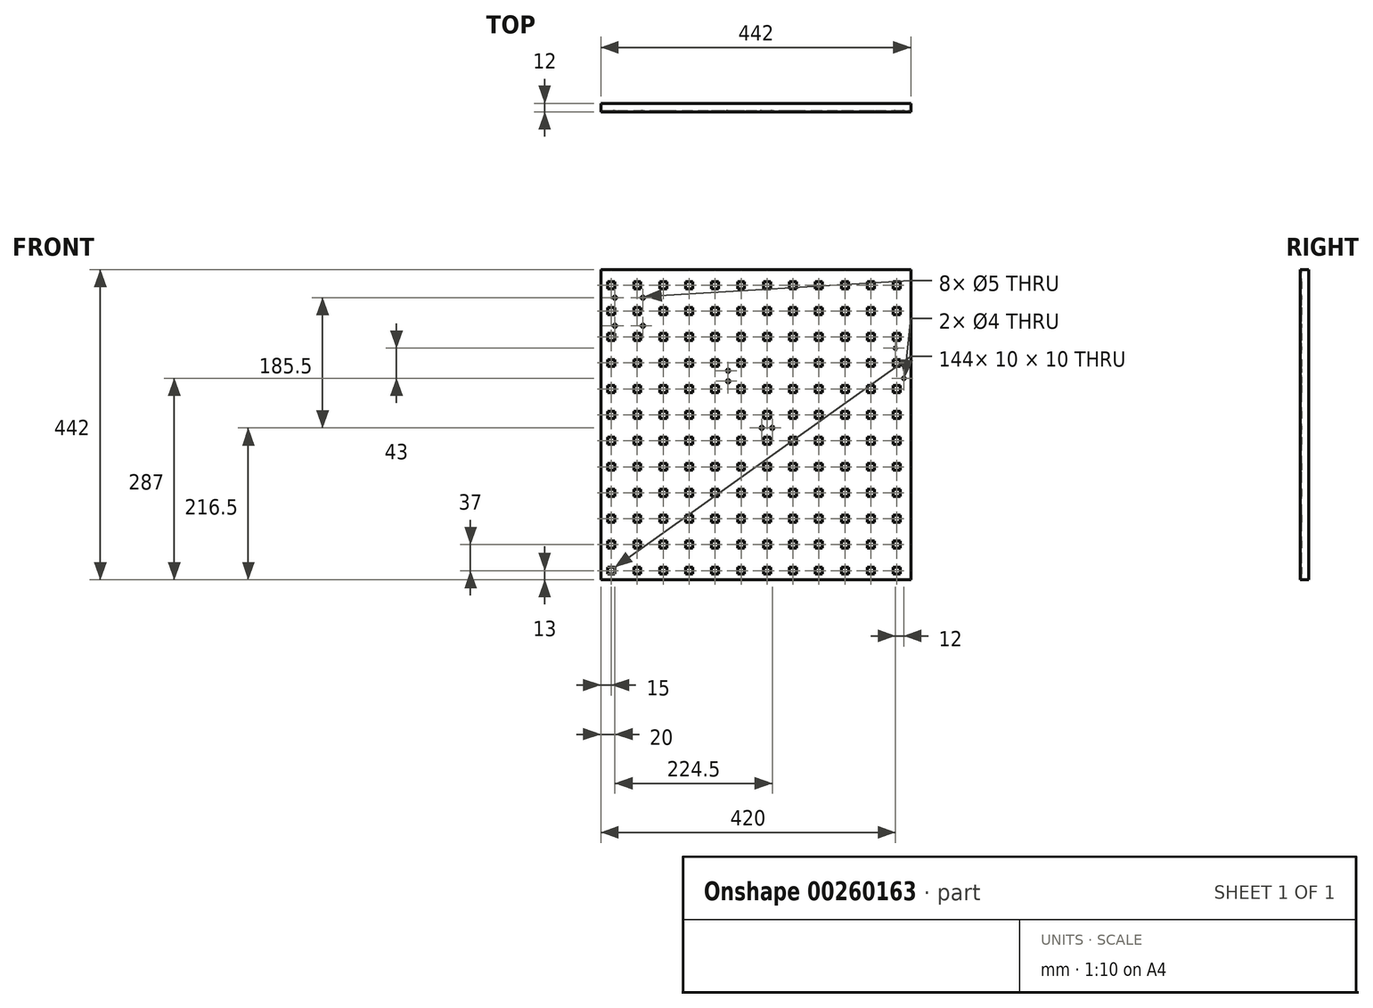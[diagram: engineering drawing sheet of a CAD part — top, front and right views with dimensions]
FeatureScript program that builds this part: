
annotation { "Feature Type Name" : "Feature", "Feature Type Description" : "" }
export const myFeature = defineFeature(function(context is Context, id is Id, definition is map)
    precondition{}
    {
        {
            var Q0;
            Q0=qCreatedBy(makeId("Front.planeOp"),FACE);
            var sketch = newSketch(context, id + "F0", { "sketchPlane" : qUnion([Q0])});
            skLineSegment(sketch, "E0.bottom", {"start": v(221, -221) * mm, "end": v(-221, -221) * mm});
            skLineSegment(sketch, "E0.top", {"start": v(221, 221) * mm, "end": v(-221, 221) * mm});
            skLineSegment(sketch, "E0.left", {"start": v(221, -221) * mm, "end": v(221, 221) * mm});
            skLineSegment(sketch, "E0.right", {"start": v(-221, -221) * mm, "end": v(-221, 221) * mm});
            skPoint(sketch, "E0.middle", {"position": v(0, 0) * mm});
            skSolve(sketch);
        }
        {
            var Q0;
            Q0=makeQuery(id+"F0.imprint","IMPRINT",FACE,{"disambiguationData":[TD([[makeQuery(id+"F0.imprint","IMPRINT",EDGE,{"derivedFrom":sQuery(id+"F0.wireOp",EDGE,"E0.bottom")}),-1.0]])]});
            extrude(context, id + "F1", {"entities" : qUnion([Q0]), "depth" : 12 * mm});
        }
        {
            var Q0;
            Q0=makeQuery(id+"F1.opExtrude","CAP_FACE",FACE,{"disambiguationData":[OSD([sQuery(id+"F0.wireOp",EDGE,"E0.bottom"),sQuery(id+"F0.wireOp",EDGE,"E0.top"),sQuery(id+"F0.wireOp",EDGE,"E0.left"),sQuery(id+"F0.wireOp",EDGE,"E0.right")])],"isStart":true});
            var sketch = newSketch(context, id + "F2", { "sketchPlane" : qUnion([Q0])});
            skLineSegment(sketch, "E1.bottom", {"start": v(220.5, -220.5) * mm, "end": v(-220.5, -220.5) * mm});
            skLineSegment(sketch, "E1.top", {"start": v(220.5, 220.5) * mm, "end": v(-220.5, 220.5) * mm});
            skLineSegment(sketch, "E1.left", {"start": v(220.5, -220.5) * mm, "end": v(220.5, 220.5) * mm});
            skLineSegment(sketch, "E1.right", {"start": v(-220.5, -220.5) * mm, "end": v(-220.5, 220.5) * mm});
            skPoint(sketch, "E1.middle", {"position": v(0, 0) * mm});
            skSolve(sketch);
        }
        {
            var Q0;
            Q0=makeQuery(id+"F2.imprint","IMPRINT",FACE,{"disambiguationData":[TD([[makeQuery(id+"F2.imprint","IMPRINT",EDGE,{"derivedFrom":sQuery(id+"F2.wireOp",EDGE,"E1.bottom")}),-1.0]])]});
            extrude(context, id + "F3", {"entities" : qUnion([Q0]), "operationType" : NewBodyOperationType.REMOVE, "oppositeDirection" : true, "depth" : 10 * mm});
        }
        {
            var Q0;
            Q0=makeQuery(id+"F1.opExtrude","CAP_FACE",FACE,{"disambiguationData":[OSD([sQuery(id+"F0.wireOp",EDGE,"E0.bottom"),sQuery(id+"F0.wireOp",EDGE,"E0.top"),sQuery(id+"F0.wireOp",EDGE,"E0.left"),sQuery(id+"F0.wireOp",EDGE,"E0.right")])],"isStart":false});
            var sketch = newSketch(context, id + "F4", { "sketchPlane" : qUnion([Q0])});
            skLineSegment(sketch, "E2.bottom", {"start": v(-201, 194) * mm, "end": v(-211, 194) * mm});
            skLineSegment(sketch, "E2.top", {"start": v(-201, 204) * mm, "end": v(-211, 204) * mm});
            skLineSegment(sketch, "E2.left", {"start": v(-201, 194) * mm, "end": v(-201, 204) * mm});
            skLineSegment(sketch, "E2.right", {"start": v(-211, 194) * mm, "end": v(-211, 204) * mm});
            skPoint(sketch, "E2.middle", {"position": v(-206, 199) * mm});
            skLineSegment(sketch, "E3.0.1.0", {"start": v(-201, 157) * mm, "end": v(-211, 157) * mm});
            skPoint(sketch, "E3.0.1.1", {"position": v(-206, 162) * mm});
            skLineSegment(sketch, "E3.0.1.2", {"start": v(-211, 157) * mm, "end": v(-211, 167) * mm});
            skLineSegment(sketch, "E3.0.1.3", {"start": v(-201, 167) * mm, "end": v(-211, 167) * mm});
            skLineSegment(sketch, "E3.0.1.4", {"start": v(-201, 157) * mm, "end": v(-201, 167) * mm});
            skLineSegment(sketch, "E3.1.0.0", {"start": v(-164, 194) * mm, "end": v(-174, 194) * mm});
            skPoint(sketch, "E3.1.0.1", {"position": v(-169, 199) * mm});
            skLineSegment(sketch, "E3.1.0.2", {"start": v(-174, 194) * mm, "end": v(-174, 204) * mm});
            skLineSegment(sketch, "E3.1.0.3", {"start": v(-164, 204) * mm, "end": v(-174, 204) * mm});
            skLineSegment(sketch, "E3.1.0.4", {"start": v(-164, 194) * mm, "end": v(-164, 204) * mm});
            skLineSegment(sketch, "E3.1.1.0", {"start": v(-164, 157) * mm, "end": v(-174, 157) * mm});
            skPoint(sketch, "E3.1.1.1", {"position": v(-169, 162) * mm});
            skLineSegment(sketch, "E3.1.1.2", {"start": v(-174, 157) * mm, "end": v(-174, 167) * mm});
            skLineSegment(sketch, "E3.1.1.3", {"start": v(-164, 167) * mm, "end": v(-174, 167) * mm});
            skLineSegment(sketch, "E3.1.1.4", {"start": v(-164, 157) * mm, "end": v(-164, 167) * mm});
            skLineSegment(sketch, "E3.2.0.0", {"start": v(-127, 194) * mm, "end": v(-137, 194) * mm});
            skPoint(sketch, "E3.2.0.1", {"position": v(-132, 199) * mm});
            skLineSegment(sketch, "E3.2.0.2", {"start": v(-137, 194) * mm, "end": v(-137, 204) * mm});
            skLineSegment(sketch, "E3.2.0.3", {"start": v(-127, 204) * mm, "end": v(-137, 204) * mm});
            skLineSegment(sketch, "E3.2.0.4", {"start": v(-127, 194) * mm, "end": v(-127, 204) * mm});
            skLineSegment(sketch, "E3.2.1.0", {"start": v(-127, 157) * mm, "end": v(-137, 157) * mm});
            skPoint(sketch, "E3.2.1.1", {"position": v(-132, 162) * mm});
            skLineSegment(sketch, "E3.2.1.2", {"start": v(-137, 157) * mm, "end": v(-137, 167) * mm});
            skLineSegment(sketch, "E3.2.1.3", {"start": v(-127, 167) * mm, "end": v(-137, 167) * mm});
            skLineSegment(sketch, "E3.2.1.4", {"start": v(-127, 157) * mm, "end": v(-127, 167) * mm});
            skLineSegment(sketch, "E3.3.0.0", {"start": v(-90, 194) * mm, "end": v(-100, 194) * mm});
            skPoint(sketch, "E3.3.0.1", {"position": v(-95, 199) * mm});
            skLineSegment(sketch, "E3.3.0.2", {"start": v(-100, 194) * mm, "end": v(-100, 204) * mm});
            skLineSegment(sketch, "E3.3.0.3", {"start": v(-90, 204) * mm, "end": v(-100, 204) * mm});
            skLineSegment(sketch, "E3.3.0.4", {"start": v(-90, 194) * mm, "end": v(-90, 204) * mm});
            skLineSegment(sketch, "E3.3.1.0", {"start": v(-90, 157) * mm, "end": v(-100, 157) * mm});
            skPoint(sketch, "E3.3.1.1", {"position": v(-95, 162) * mm});
            skLineSegment(sketch, "E3.3.1.2", {"start": v(-100, 157) * mm, "end": v(-100, 167) * mm});
            skLineSegment(sketch, "E3.3.1.3", {"start": v(-90, 167) * mm, "end": v(-100, 167) * mm});
            skLineSegment(sketch, "E3.3.1.4", {"start": v(-90, 157) * mm, "end": v(-90, 167) * mm});
            skLineSegment(sketch, "E3.4.0.0", {"start": v(-53, 194) * mm, "end": v(-63, 194) * mm});
            skPoint(sketch, "E3.4.0.1", {"position": v(-58, 199) * mm});
            skLineSegment(sketch, "E3.4.0.2", {"start": v(-63, 194) * mm, "end": v(-63, 204) * mm});
            skLineSegment(sketch, "E3.4.0.3", {"start": v(-53, 204) * mm, "end": v(-63, 204) * mm});
            skLineSegment(sketch, "E3.4.0.4", {"start": v(-53, 194) * mm, "end": v(-53, 204) * mm});
            skLineSegment(sketch, "E3.4.1.0", {"start": v(-53, 157) * mm, "end": v(-63, 157) * mm});
            skPoint(sketch, "E3.4.1.1", {"position": v(-58, 162) * mm});
            skLineSegment(sketch, "E3.4.1.2", {"start": v(-63, 157) * mm, "end": v(-63, 167) * mm});
            skLineSegment(sketch, "E3.4.1.3", {"start": v(-53, 167) * mm, "end": v(-63, 167) * mm});
            skLineSegment(sketch, "E3.4.1.4", {"start": v(-53, 157) * mm, "end": v(-53, 167) * mm});
            skLineSegment(sketch, "E3.5.0.0", {"start": v(-16, 194) * mm, "end": v(-26, 194) * mm});
            skPoint(sketch, "E3.5.0.1", {"position": v(-21, 199) * mm});
            skLineSegment(sketch, "E3.5.0.2", {"start": v(-26, 194) * mm, "end": v(-26, 204) * mm});
            skLineSegment(sketch, "E3.5.0.3", {"start": v(-16, 204) * mm, "end": v(-26, 204) * mm});
            skLineSegment(sketch, "E3.5.0.4", {"start": v(-16, 194) * mm, "end": v(-16, 204) * mm});
            skLineSegment(sketch, "E3.5.1.0", {"start": v(-16, 157) * mm, "end": v(-26, 157) * mm});
            skPoint(sketch, "E3.5.1.1", {"position": v(-21, 162) * mm});
            skLineSegment(sketch, "E3.5.1.2", {"start": v(-26, 157) * mm, "end": v(-26, 167) * mm});
            skLineSegment(sketch, "E3.5.1.3", {"start": v(-16, 167) * mm, "end": v(-26, 167) * mm});
            skLineSegment(sketch, "E3.5.1.4", {"start": v(-16, 157) * mm, "end": v(-16, 167) * mm});
            skLineSegment(sketch, "E3.6.0.0", {"start": v(21, 194) * mm, "end": v(11, 194) * mm});
            skPoint(sketch, "E3.6.0.1", {"position": v(16, 199) * mm});
            skLineSegment(sketch, "E3.6.0.2", {"start": v(11, 194) * mm, "end": v(11, 204) * mm});
            skLineSegment(sketch, "E3.6.0.3", {"start": v(21, 204) * mm, "end": v(11, 204) * mm});
            skLineSegment(sketch, "E3.6.0.4", {"start": v(21, 194) * mm, "end": v(21, 204) * mm});
            skLineSegment(sketch, "E3.6.1.0", {"start": v(21, 157) * mm, "end": v(11, 157) * mm});
            skPoint(sketch, "E3.6.1.1", {"position": v(16, 162) * mm});
            skLineSegment(sketch, "E3.6.1.2", {"start": v(11, 157) * mm, "end": v(11, 167) * mm});
            skLineSegment(sketch, "E3.6.1.3", {"start": v(21, 167) * mm, "end": v(11, 167) * mm});
            skLineSegment(sketch, "E3.6.1.4", {"start": v(21, 157) * mm, "end": v(21, 167) * mm});
            skLineSegment(sketch, "E3.7.0.0", {"start": v(58, 194) * mm, "end": v(48, 194) * mm});
            skPoint(sketch, "E3.7.0.1", {"position": v(53, 199) * mm});
            skLineSegment(sketch, "E3.7.0.2", {"start": v(48, 194) * mm, "end": v(48, 204) * mm});
            skLineSegment(sketch, "E3.7.0.3", {"start": v(58, 204) * mm, "end": v(48, 204) * mm});
            skLineSegment(sketch, "E3.7.0.4", {"start": v(58, 194) * mm, "end": v(58, 204) * mm});
            skLineSegment(sketch, "E3.7.1.0", {"start": v(58, 157) * mm, "end": v(48, 157) * mm});
            skPoint(sketch, "E3.7.1.1", {"position": v(53, 162) * mm});
            skLineSegment(sketch, "E3.7.1.2", {"start": v(48, 157) * mm, "end": v(48, 167) * mm});
            skLineSegment(sketch, "E3.7.1.3", {"start": v(58, 167) * mm, "end": v(48, 167) * mm});
            skLineSegment(sketch, "E3.7.1.4", {"start": v(58, 157) * mm, "end": v(58, 167) * mm});
            skLineSegment(sketch, "E3.8.0.0", {"start": v(95, 194) * mm, "end": v(85, 194) * mm});
            skPoint(sketch, "E3.8.0.1", {"position": v(90, 199) * mm});
            skLineSegment(sketch, "E3.8.0.2", {"start": v(85, 194) * mm, "end": v(85, 204) * mm});
            skLineSegment(sketch, "E3.8.0.3", {"start": v(95, 204) * mm, "end": v(85, 204) * mm});
            skLineSegment(sketch, "E3.8.0.4", {"start": v(95, 194) * mm, "end": v(95, 204) * mm});
            skLineSegment(sketch, "E3.8.1.0", {"start": v(95, 157) * mm, "end": v(85, 157) * mm});
            skPoint(sketch, "E3.8.1.1", {"position": v(90, 162) * mm});
            skLineSegment(sketch, "E3.8.1.2", {"start": v(85, 157) * mm, "end": v(85, 167) * mm});
            skLineSegment(sketch, "E3.8.1.3", {"start": v(95, 167) * mm, "end": v(85, 167) * mm});
            skLineSegment(sketch, "E3.8.1.4", {"start": v(95, 157) * mm, "end": v(95, 167) * mm});
            skLineSegment(sketch, "E3.9.0.0", {"start": v(132, 194) * mm, "end": v(122, 194) * mm});
            skPoint(sketch, "E3.9.0.1", {"position": v(127, 199) * mm});
            skLineSegment(sketch, "E3.9.0.2", {"start": v(122, 194) * mm, "end": v(122, 204) * mm});
            skLineSegment(sketch, "E3.9.0.3", {"start": v(132, 204) * mm, "end": v(122, 204) * mm});
            skLineSegment(sketch, "E3.9.0.4", {"start": v(132, 194) * mm, "end": v(132, 204) * mm});
            skLineSegment(sketch, "E3.9.1.0", {"start": v(132, 157) * mm, "end": v(122, 157) * mm});
            skPoint(sketch, "E3.9.1.1", {"position": v(127, 162) * mm});
            skLineSegment(sketch, "E3.9.1.2", {"start": v(122, 157) * mm, "end": v(122, 167) * mm});
            skLineSegment(sketch, "E3.9.1.3", {"start": v(132, 167) * mm, "end": v(122, 167) * mm});
            skLineSegment(sketch, "E3.9.1.4", {"start": v(132, 157) * mm, "end": v(132, 167) * mm});
            skLineSegment(sketch, "E3.10.0.0", {"start": v(169, 194) * mm, "end": v(159, 194) * mm});
            skPoint(sketch, "E3.10.0.1", {"position": v(164, 199) * mm});
            skLineSegment(sketch, "E3.10.0.2", {"start": v(159, 194) * mm, "end": v(159, 204) * mm});
            skLineSegment(sketch, "E3.10.0.3", {"start": v(169, 204) * mm, "end": v(159, 204) * mm});
            skLineSegment(sketch, "E3.10.0.4", {"start": v(169, 194) * mm, "end": v(169, 204) * mm});
            skLineSegment(sketch, "E3.10.1.0", {"start": v(169, 157) * mm, "end": v(159, 157) * mm});
            skPoint(sketch, "E3.10.1.1", {"position": v(164, 162) * mm});
            skLineSegment(sketch, "E3.10.1.2", {"start": v(159, 157) * mm, "end": v(159, 167) * mm});
            skLineSegment(sketch, "E3.10.1.3", {"start": v(169, 167) * mm, "end": v(159, 167) * mm});
            skLineSegment(sketch, "E3.10.1.4", {"start": v(169, 157) * mm, "end": v(169, 167) * mm});
            skLineSegment(sketch, "E3.11.0.0", {"start": v(206, 194) * mm, "end": v(196, 194) * mm});
            skPoint(sketch, "E3.11.0.1", {"position": v(201, 199) * mm});
            skLineSegment(sketch, "E3.11.0.2", {"start": v(196, 194) * mm, "end": v(196, 204) * mm});
            skLineSegment(sketch, "E3.11.0.3", {"start": v(206, 204) * mm, "end": v(196, 204) * mm});
            skLineSegment(sketch, "E3.11.0.4", {"start": v(206, 194) * mm, "end": v(206, 204) * mm});
            skLineSegment(sketch, "E3.11.1.0", {"start": v(206, 157) * mm, "end": v(196, 157) * mm});
            skPoint(sketch, "E3.11.1.1", {"position": v(201, 162) * mm});
            skLineSegment(sketch, "E3.11.1.2", {"start": v(196, 157) * mm, "end": v(196, 167) * mm});
            skLineSegment(sketch, "E3.11.1.3", {"start": v(206, 167) * mm, "end": v(196, 167) * mm});
            skLineSegment(sketch, "E3.11.1.4", {"start": v(206, 157) * mm, "end": v(206, 167) * mm});
            skLineSegment(sketch, "E3.direction1", {"start": v(-211, 194) * mm, "end": v(-174, 194) * mm, "construction": true});
            skLineSegment(sketch, "E3.direction2", {"start": v(-211, 194) * mm, "end": v(-211, 157) * mm, "construction": true});
            skLineSegment(sketch, "E4.0.0.2", {"start": v(-201, 120) * mm, "end": v(-211, 120) * mm});
            skPoint(sketch, "E4.3.0.2", {"position": v(-206, 125) * mm});
            skLineSegment(sketch, "E4.4.0.2", {"start": v(-211, 120) * mm, "end": v(-211, 130) * mm});
            skLineSegment(sketch, "E4.7.0.2", {"start": v(-201, 130) * mm, "end": v(-211, 130) * mm});
            skLineSegment(sketch, "E4.10.0.2", {"start": v(-201, 120) * mm, "end": v(-201, 130) * mm});
            skLineSegment(sketch, "E4.0.0.3", {"start": v(-201, 83) * mm, "end": v(-211, 83) * mm});
            skPoint(sketch, "E4.3.0.3", {"position": v(-206, 88) * mm});
            skLineSegment(sketch, "E4.4.0.3", {"start": v(-211, 83) * mm, "end": v(-211, 93) * mm});
            skLineSegment(sketch, "E4.7.0.3", {"start": v(-201, 93) * mm, "end": v(-211, 93) * mm});
            skLineSegment(sketch, "E4.10.0.3", {"start": v(-201, 83) * mm, "end": v(-201, 93) * mm});
            skLineSegment(sketch, "E4.0.0.4", {"start": v(-201, 46) * mm, "end": v(-211, 46) * mm});
            skPoint(sketch, "E4.3.0.4", {"position": v(-206, 51) * mm});
            skLineSegment(sketch, "E4.4.0.4", {"start": v(-211, 46) * mm, "end": v(-211, 56) * mm});
            skLineSegment(sketch, "E4.7.0.4", {"start": v(-201, 56) * mm, "end": v(-211, 56) * mm});
            skLineSegment(sketch, "E4.10.0.4", {"start": v(-201, 46) * mm, "end": v(-201, 56) * mm});
            skLineSegment(sketch, "E4.0.0.5", {"start": v(-201, 9) * mm, "end": v(-211, 9) * mm});
            skPoint(sketch, "E4.3.0.5", {"position": v(-206, 14) * mm});
            skLineSegment(sketch, "E4.4.0.5", {"start": v(-211, 9) * mm, "end": v(-211, 19) * mm});
            skLineSegment(sketch, "E4.7.0.5", {"start": v(-201, 19) * mm, "end": v(-211, 19) * mm});
            skLineSegment(sketch, "E4.10.0.5", {"start": v(-201, 9) * mm, "end": v(-201, 19) * mm});
            skLineSegment(sketch, "E4.0.0.6", {"start": v(-201, -28) * mm, "end": v(-211, -28) * mm});
            skPoint(sketch, "E4.3.0.6", {"position": v(-206, -23) * mm});
            skLineSegment(sketch, "E4.4.0.6", {"start": v(-211, -28) * mm, "end": v(-211, -18) * mm});
            skLineSegment(sketch, "E4.7.0.6", {"start": v(-201, -18) * mm, "end": v(-211, -18) * mm});
            skLineSegment(sketch, "E4.10.0.6", {"start": v(-201, -28) * mm, "end": v(-201, -18) * mm});
            skLineSegment(sketch, "E4.0.0.7", {"start": v(-201, -65) * mm, "end": v(-211, -65) * mm});
            skPoint(sketch, "E4.3.0.7", {"position": v(-206, -60) * mm});
            skLineSegment(sketch, "E4.4.0.7", {"start": v(-211, -65) * mm, "end": v(-211, -55) * mm});
            skLineSegment(sketch, "E4.7.0.7", {"start": v(-201, -55) * mm, "end": v(-211, -55) * mm});
            skLineSegment(sketch, "E4.10.0.7", {"start": v(-201, -65) * mm, "end": v(-201, -55) * mm});
            skLineSegment(sketch, "E4.0.0.8", {"start": v(-201, -102) * mm, "end": v(-211, -102) * mm});
            skPoint(sketch, "E4.3.0.8", {"position": v(-206, -97) * mm});
            skLineSegment(sketch, "E4.4.0.8", {"start": v(-211, -102) * mm, "end": v(-211, -92) * mm});
            skLineSegment(sketch, "E4.7.0.8", {"start": v(-201, -92) * mm, "end": v(-211, -92) * mm});
            skLineSegment(sketch, "E4.10.0.8", {"start": v(-201, -102) * mm, "end": v(-201, -92) * mm});
            skLineSegment(sketch, "E4.0.0.9", {"start": v(-201, -139) * mm, "end": v(-211, -139) * mm});
            skPoint(sketch, "E4.3.0.9", {"position": v(-206, -134) * mm});
            skLineSegment(sketch, "E4.4.0.9", {"start": v(-211, -139) * mm, "end": v(-211, -129) * mm});
            skLineSegment(sketch, "E4.7.0.9", {"start": v(-201, -129) * mm, "end": v(-211, -129) * mm});
            skLineSegment(sketch, "E4.10.0.9", {"start": v(-201, -139) * mm, "end": v(-201, -129) * mm});
            skLineSegment(sketch, "E4.0.0.10", {"start": v(-201, -176) * mm, "end": v(-211, -176) * mm});
            skPoint(sketch, "E4.3.0.10", {"position": v(-206, -171) * mm});
            skLineSegment(sketch, "E4.4.0.10", {"start": v(-211, -176) * mm, "end": v(-211, -166) * mm});
            skLineSegment(sketch, "E4.7.0.10", {"start": v(-201, -166) * mm, "end": v(-211, -166) * mm});
            skLineSegment(sketch, "E4.10.0.10", {"start": v(-201, -176) * mm, "end": v(-201, -166) * mm});
            skLineSegment(sketch, "E4.0.0.11", {"start": v(-201, -213) * mm, "end": v(-211, -213) * mm});
            skPoint(sketch, "E4.3.0.11", {"position": v(-206, -208) * mm});
            skLineSegment(sketch, "E4.4.0.11", {"start": v(-211, -213) * mm, "end": v(-211, -203) * mm});
            skLineSegment(sketch, "E4.7.0.11", {"start": v(-201, -203) * mm, "end": v(-211, -203) * mm});
            skLineSegment(sketch, "E4.10.0.11", {"start": v(-201, -213) * mm, "end": v(-201, -203) * mm});
            skLineSegment(sketch, "E4.0.1.2", {"start": v(-164, 120) * mm, "end": v(-174, 120) * mm});
            skPoint(sketch, "E4.3.1.2", {"position": v(-169, 125) * mm});
            skLineSegment(sketch, "E4.4.1.2", {"start": v(-174, 120) * mm, "end": v(-174, 130) * mm});
            skLineSegment(sketch, "E4.7.1.2", {"start": v(-164, 130) * mm, "end": v(-174, 130) * mm});
            skLineSegment(sketch, "E4.10.1.2", {"start": v(-164, 120) * mm, "end": v(-164, 130) * mm});
            skLineSegment(sketch, "E4.0.1.3", {"start": v(-164, 83) * mm, "end": v(-174, 83) * mm});
            skPoint(sketch, "E4.3.1.3", {"position": v(-169, 88) * mm});
            skLineSegment(sketch, "E4.4.1.3", {"start": v(-174, 83) * mm, "end": v(-174, 93) * mm});
            skLineSegment(sketch, "E4.7.1.3", {"start": v(-164, 93) * mm, "end": v(-174, 93) * mm});
            skLineSegment(sketch, "E4.10.1.3", {"start": v(-164, 83) * mm, "end": v(-164, 93) * mm});
            skLineSegment(sketch, "E4.0.1.4", {"start": v(-164, 46) * mm, "end": v(-174, 46) * mm});
            skPoint(sketch, "E4.3.1.4", {"position": v(-169, 51) * mm});
            skLineSegment(sketch, "E4.4.1.4", {"start": v(-174, 46) * mm, "end": v(-174, 56) * mm});
            skLineSegment(sketch, "E4.7.1.4", {"start": v(-164, 56) * mm, "end": v(-174, 56) * mm});
            skLineSegment(sketch, "E4.10.1.4", {"start": v(-164, 46) * mm, "end": v(-164, 56) * mm});
            skLineSegment(sketch, "E4.0.1.5", {"start": v(-164, 9) * mm, "end": v(-174, 9) * mm});
            skPoint(sketch, "E4.3.1.5", {"position": v(-169, 14) * mm});
            skLineSegment(sketch, "E4.4.1.5", {"start": v(-174, 9) * mm, "end": v(-174, 19) * mm});
            skLineSegment(sketch, "E4.7.1.5", {"start": v(-164, 19) * mm, "end": v(-174, 19) * mm});
            skLineSegment(sketch, "E4.10.1.5", {"start": v(-164, 9) * mm, "end": v(-164, 19) * mm});
            skLineSegment(sketch, "E4.0.1.6", {"start": v(-164, -28) * mm, "end": v(-174, -28) * mm});
            skPoint(sketch, "E4.3.1.6", {"position": v(-169, -23) * mm});
            skLineSegment(sketch, "E4.4.1.6", {"start": v(-174, -28) * mm, "end": v(-174, -18) * mm});
            skLineSegment(sketch, "E4.7.1.6", {"start": v(-164, -18) * mm, "end": v(-174, -18) * mm});
            skLineSegment(sketch, "E4.10.1.6", {"start": v(-164, -28) * mm, "end": v(-164, -18) * mm});
            skLineSegment(sketch, "E4.0.1.7", {"start": v(-164, -65) * mm, "end": v(-174, -65) * mm});
            skPoint(sketch, "E4.3.1.7", {"position": v(-169, -60) * mm});
            skLineSegment(sketch, "E4.4.1.7", {"start": v(-174, -65) * mm, "end": v(-174, -55) * mm});
            skLineSegment(sketch, "E4.7.1.7", {"start": v(-164, -55) * mm, "end": v(-174, -55) * mm});
            skLineSegment(sketch, "E4.10.1.7", {"start": v(-164, -65) * mm, "end": v(-164, -55) * mm});
            skLineSegment(sketch, "E4.0.1.8", {"start": v(-164, -102) * mm, "end": v(-174, -102) * mm});
            skPoint(sketch, "E4.3.1.8", {"position": v(-169, -97) * mm});
            skLineSegment(sketch, "E4.4.1.8", {"start": v(-174, -102) * mm, "end": v(-174, -92) * mm});
            skLineSegment(sketch, "E4.7.1.8", {"start": v(-164, -92) * mm, "end": v(-174, -92) * mm});
            skLineSegment(sketch, "E4.10.1.8", {"start": v(-164, -102) * mm, "end": v(-164, -92) * mm});
            skLineSegment(sketch, "E4.0.1.9", {"start": v(-164, -139) * mm, "end": v(-174, -139) * mm});
            skPoint(sketch, "E4.3.1.9", {"position": v(-169, -134) * mm});
            skLineSegment(sketch, "E4.4.1.9", {"start": v(-174, -139) * mm, "end": v(-174, -129) * mm});
            skLineSegment(sketch, "E4.7.1.9", {"start": v(-164, -129) * mm, "end": v(-174, -129) * mm});
            skLineSegment(sketch, "E4.10.1.9", {"start": v(-164, -139) * mm, "end": v(-164, -129) * mm});
            skLineSegment(sketch, "E4.0.1.10", {"start": v(-164, -176) * mm, "end": v(-174, -176) * mm});
            skPoint(sketch, "E4.3.1.10", {"position": v(-169, -171) * mm});
            skLineSegment(sketch, "E4.4.1.10", {"start": v(-174, -176) * mm, "end": v(-174, -166) * mm});
            skLineSegment(sketch, "E4.7.1.10", {"start": v(-164, -166) * mm, "end": v(-174, -166) * mm});
            skLineSegment(sketch, "E4.10.1.10", {"start": v(-164, -176) * mm, "end": v(-164, -166) * mm});
            skLineSegment(sketch, "E4.0.1.11", {"start": v(-164, -213) * mm, "end": v(-174, -213) * mm});
            skPoint(sketch, "E4.3.1.11", {"position": v(-169, -208) * mm});
            skLineSegment(sketch, "E4.4.1.11", {"start": v(-174, -213) * mm, "end": v(-174, -203) * mm});
            skLineSegment(sketch, "E4.7.1.11", {"start": v(-164, -203) * mm, "end": v(-174, -203) * mm});
            skLineSegment(sketch, "E4.10.1.11", {"start": v(-164, -213) * mm, "end": v(-164, -203) * mm});
            skLineSegment(sketch, "E4.0.2.2", {"start": v(-127, 120) * mm, "end": v(-137, 120) * mm});
            skPoint(sketch, "E4.3.2.2", {"position": v(-132, 125) * mm});
            skLineSegment(sketch, "E4.4.2.2", {"start": v(-137, 120) * mm, "end": v(-137, 130) * mm});
            skLineSegment(sketch, "E4.7.2.2", {"start": v(-127, 130) * mm, "end": v(-137, 130) * mm});
            skLineSegment(sketch, "E4.10.2.2", {"start": v(-127, 120) * mm, "end": v(-127, 130) * mm});
            skLineSegment(sketch, "E4.0.2.3", {"start": v(-127, 83) * mm, "end": v(-137, 83) * mm});
            skPoint(sketch, "E4.3.2.3", {"position": v(-132, 88) * mm});
            skLineSegment(sketch, "E4.4.2.3", {"start": v(-137, 83) * mm, "end": v(-137, 93) * mm});
            skLineSegment(sketch, "E4.7.2.3", {"start": v(-127, 93) * mm, "end": v(-137, 93) * mm});
            skLineSegment(sketch, "E4.10.2.3", {"start": v(-127, 83) * mm, "end": v(-127, 93) * mm});
            skLineSegment(sketch, "E4.0.2.4", {"start": v(-127, 46) * mm, "end": v(-137, 46) * mm});
            skPoint(sketch, "E4.3.2.4", {"position": v(-132, 51) * mm});
            skLineSegment(sketch, "E4.4.2.4", {"start": v(-137, 46) * mm, "end": v(-137, 56) * mm});
            skLineSegment(sketch, "E4.7.2.4", {"start": v(-127, 56) * mm, "end": v(-137, 56) * mm});
            skLineSegment(sketch, "E4.10.2.4", {"start": v(-127, 46) * mm, "end": v(-127, 56) * mm});
            skLineSegment(sketch, "E4.0.2.5", {"start": v(-127, 9) * mm, "end": v(-137, 9) * mm});
            skPoint(sketch, "E4.3.2.5", {"position": v(-132, 14) * mm});
            skLineSegment(sketch, "E4.4.2.5", {"start": v(-137, 9) * mm, "end": v(-137, 19) * mm});
            skLineSegment(sketch, "E4.7.2.5", {"start": v(-127, 19) * mm, "end": v(-137, 19) * mm});
            skLineSegment(sketch, "E4.10.2.5", {"start": v(-127, 9) * mm, "end": v(-127, 19) * mm});
            skLineSegment(sketch, "E4.0.2.6", {"start": v(-127, -28) * mm, "end": v(-137, -28) * mm});
            skPoint(sketch, "E4.3.2.6", {"position": v(-132, -23) * mm});
            skLineSegment(sketch, "E4.4.2.6", {"start": v(-137, -28) * mm, "end": v(-137, -18) * mm});
            skLineSegment(sketch, "E4.7.2.6", {"start": v(-127, -18) * mm, "end": v(-137, -18) * mm});
            skLineSegment(sketch, "E4.10.2.6", {"start": v(-127, -28) * mm, "end": v(-127, -18) * mm});
            skLineSegment(sketch, "E4.0.2.7", {"start": v(-127, -65) * mm, "end": v(-137, -65) * mm});
            skPoint(sketch, "E4.3.2.7", {"position": v(-132, -60) * mm});
            skLineSegment(sketch, "E4.4.2.7", {"start": v(-137, -65) * mm, "end": v(-137, -55) * mm});
            skLineSegment(sketch, "E4.7.2.7", {"start": v(-127, -55) * mm, "end": v(-137, -55) * mm});
            skLineSegment(sketch, "E4.10.2.7", {"start": v(-127, -65) * mm, "end": v(-127, -55) * mm});
            skLineSegment(sketch, "E4.0.2.8", {"start": v(-127, -102) * mm, "end": v(-137, -102) * mm});
            skPoint(sketch, "E4.3.2.8", {"position": v(-132, -97) * mm});
            skLineSegment(sketch, "E4.4.2.8", {"start": v(-137, -102) * mm, "end": v(-137, -92) * mm});
            skLineSegment(sketch, "E4.7.2.8", {"start": v(-127, -92) * mm, "end": v(-137, -92) * mm});
            skLineSegment(sketch, "E4.10.2.8", {"start": v(-127, -102) * mm, "end": v(-127, -92) * mm});
            skLineSegment(sketch, "E4.0.2.9", {"start": v(-127, -139) * mm, "end": v(-137, -139) * mm});
            skPoint(sketch, "E4.3.2.9", {"position": v(-132, -134) * mm});
            skLineSegment(sketch, "E4.4.2.9", {"start": v(-137, -139) * mm, "end": v(-137, -129) * mm});
            skLineSegment(sketch, "E4.7.2.9", {"start": v(-127, -129) * mm, "end": v(-137, -129) * mm});
            skLineSegment(sketch, "E4.10.2.9", {"start": v(-127, -139) * mm, "end": v(-127, -129) * mm});
            skLineSegment(sketch, "E4.0.2.10", {"start": v(-127, -176) * mm, "end": v(-137, -176) * mm});
            skPoint(sketch, "E4.3.2.10", {"position": v(-132, -171) * mm});
            skLineSegment(sketch, "E4.4.2.10", {"start": v(-137, -176) * mm, "end": v(-137, -166) * mm});
            skLineSegment(sketch, "E4.7.2.10", {"start": v(-127, -166) * mm, "end": v(-137, -166) * mm});
            skLineSegment(sketch, "E4.10.2.10", {"start": v(-127, -176) * mm, "end": v(-127, -166) * mm});
            skLineSegment(sketch, "E4.0.2.11", {"start": v(-127, -213) * mm, "end": v(-137, -213) * mm});
            skPoint(sketch, "E4.3.2.11", {"position": v(-132, -208) * mm});
            skLineSegment(sketch, "E4.4.2.11", {"start": v(-137, -213) * mm, "end": v(-137, -203) * mm});
            skLineSegment(sketch, "E4.7.2.11", {"start": v(-127, -203) * mm, "end": v(-137, -203) * mm});
            skLineSegment(sketch, "E4.10.2.11", {"start": v(-127, -213) * mm, "end": v(-127, -203) * mm});
            skLineSegment(sketch, "E4.0.3.2", {"start": v(-90, 120) * mm, "end": v(-100, 120) * mm});
            skPoint(sketch, "E4.3.3.2", {"position": v(-95, 125) * mm});
            skLineSegment(sketch, "E4.4.3.2", {"start": v(-100, 120) * mm, "end": v(-100, 130) * mm});
            skLineSegment(sketch, "E4.7.3.2", {"start": v(-90, 130) * mm, "end": v(-100, 130) * mm});
            skLineSegment(sketch, "E4.10.3.2", {"start": v(-90, 120) * mm, "end": v(-90, 130) * mm});
            skLineSegment(sketch, "E4.0.3.3", {"start": v(-90, 83) * mm, "end": v(-100, 83) * mm});
            skPoint(sketch, "E4.3.3.3", {"position": v(-95, 88) * mm});
            skLineSegment(sketch, "E4.4.3.3", {"start": v(-100, 83) * mm, "end": v(-100, 93) * mm});
            skLineSegment(sketch, "E4.7.3.3", {"start": v(-90, 93) * mm, "end": v(-100, 93) * mm});
            skLineSegment(sketch, "E4.10.3.3", {"start": v(-90, 83) * mm, "end": v(-90, 93) * mm});
            skLineSegment(sketch, "E4.0.3.4", {"start": v(-90, 46) * mm, "end": v(-100, 46) * mm});
            skPoint(sketch, "E4.3.3.4", {"position": v(-95, 51) * mm});
            skLineSegment(sketch, "E4.4.3.4", {"start": v(-100, 46) * mm, "end": v(-100, 56) * mm});
            skLineSegment(sketch, "E4.7.3.4", {"start": v(-90, 56) * mm, "end": v(-100, 56) * mm});
            skLineSegment(sketch, "E4.10.3.4", {"start": v(-90, 46) * mm, "end": v(-90, 56) * mm});
            skLineSegment(sketch, "E4.0.3.5", {"start": v(-90, 9) * mm, "end": v(-100, 9) * mm});
            skPoint(sketch, "E4.3.3.5", {"position": v(-95, 14) * mm});
            skLineSegment(sketch, "E4.4.3.5", {"start": v(-100, 9) * mm, "end": v(-100, 19) * mm});
            skLineSegment(sketch, "E4.7.3.5", {"start": v(-90, 19) * mm, "end": v(-100, 19) * mm});
            skLineSegment(sketch, "E4.10.3.5", {"start": v(-90, 9) * mm, "end": v(-90, 19) * mm});
            skLineSegment(sketch, "E4.0.3.6", {"start": v(-90, -28) * mm, "end": v(-100, -28) * mm});
            skPoint(sketch, "E4.3.3.6", {"position": v(-95, -23) * mm});
            skLineSegment(sketch, "E4.4.3.6", {"start": v(-100, -28) * mm, "end": v(-100, -18) * mm});
            skLineSegment(sketch, "E4.7.3.6", {"start": v(-90, -18) * mm, "end": v(-100, -18) * mm});
            skLineSegment(sketch, "E4.10.3.6", {"start": v(-90, -28) * mm, "end": v(-90, -18) * mm});
            skLineSegment(sketch, "E4.0.3.7", {"start": v(-90, -65) * mm, "end": v(-100, -65) * mm});
            skPoint(sketch, "E4.3.3.7", {"position": v(-95, -60) * mm});
            skLineSegment(sketch, "E4.4.3.7", {"start": v(-100, -65) * mm, "end": v(-100, -55) * mm});
            skLineSegment(sketch, "E4.7.3.7", {"start": v(-90, -55) * mm, "end": v(-100, -55) * mm});
            skLineSegment(sketch, "E4.10.3.7", {"start": v(-90, -65) * mm, "end": v(-90, -55) * mm});
            skLineSegment(sketch, "E4.0.3.8", {"start": v(-90, -102) * mm, "end": v(-100, -102) * mm});
            skPoint(sketch, "E4.3.3.8", {"position": v(-95, -97) * mm});
            skLineSegment(sketch, "E4.4.3.8", {"start": v(-100, -102) * mm, "end": v(-100, -92) * mm});
            skLineSegment(sketch, "E4.7.3.8", {"start": v(-90, -92) * mm, "end": v(-100, -92) * mm});
            skLineSegment(sketch, "E4.10.3.8", {"start": v(-90, -102) * mm, "end": v(-90, -92) * mm});
            skLineSegment(sketch, "E4.0.3.9", {"start": v(-90, -139) * mm, "end": v(-100, -139) * mm});
            skPoint(sketch, "E4.3.3.9", {"position": v(-95, -134) * mm});
            skLineSegment(sketch, "E4.4.3.9", {"start": v(-100, -139) * mm, "end": v(-100, -129) * mm});
            skLineSegment(sketch, "E4.7.3.9", {"start": v(-90, -129) * mm, "end": v(-100, -129) * mm});
            skLineSegment(sketch, "E4.10.3.9", {"start": v(-90, -139) * mm, "end": v(-90, -129) * mm});
            skLineSegment(sketch, "E4.0.3.10", {"start": v(-90, -176) * mm, "end": v(-100, -176) * mm});
            skPoint(sketch, "E4.3.3.10", {"position": v(-95, -171) * mm});
            skLineSegment(sketch, "E4.4.3.10", {"start": v(-100, -176) * mm, "end": v(-100, -166) * mm});
            skLineSegment(sketch, "E4.7.3.10", {"start": v(-90, -166) * mm, "end": v(-100, -166) * mm});
            skLineSegment(sketch, "E4.10.3.10", {"start": v(-90, -176) * mm, "end": v(-90, -166) * mm});
            skLineSegment(sketch, "E4.0.3.11", {"start": v(-90, -213) * mm, "end": v(-100, -213) * mm});
            skPoint(sketch, "E4.3.3.11", {"position": v(-95, -208) * mm});
            skLineSegment(sketch, "E4.4.3.11", {"start": v(-100, -213) * mm, "end": v(-100, -203) * mm});
            skLineSegment(sketch, "E4.7.3.11", {"start": v(-90, -203) * mm, "end": v(-100, -203) * mm});
            skLineSegment(sketch, "E4.10.3.11", {"start": v(-90, -213) * mm, "end": v(-90, -203) * mm});
            skLineSegment(sketch, "E4.0.4.2", {"start": v(-53, 120) * mm, "end": v(-63, 120) * mm});
            skPoint(sketch, "E4.3.4.2", {"position": v(-58, 125) * mm});
            skLineSegment(sketch, "E4.4.4.2", {"start": v(-63, 120) * mm, "end": v(-63, 130) * mm});
            skLineSegment(sketch, "E4.7.4.2", {"start": v(-53, 130) * mm, "end": v(-63, 130) * mm});
            skLineSegment(sketch, "E4.10.4.2", {"start": v(-53, 120) * mm, "end": v(-53, 130) * mm});
            skLineSegment(sketch, "E4.0.4.3", {"start": v(-53, 83) * mm, "end": v(-63, 83) * mm});
            skPoint(sketch, "E4.3.4.3", {"position": v(-58, 88) * mm});
            skLineSegment(sketch, "E4.4.4.3", {"start": v(-63, 83) * mm, "end": v(-63, 93) * mm});
            skLineSegment(sketch, "E4.7.4.3", {"start": v(-53, 93) * mm, "end": v(-63, 93) * mm});
            skLineSegment(sketch, "E4.10.4.3", {"start": v(-53, 83) * mm, "end": v(-53, 93) * mm});
            skLineSegment(sketch, "E4.0.4.4", {"start": v(-53, 46) * mm, "end": v(-63, 46) * mm});
            skPoint(sketch, "E4.3.4.4", {"position": v(-58, 51) * mm});
            skLineSegment(sketch, "E4.4.4.4", {"start": v(-63, 46) * mm, "end": v(-63, 56) * mm});
            skLineSegment(sketch, "E4.7.4.4", {"start": v(-53, 56) * mm, "end": v(-63, 56) * mm});
            skLineSegment(sketch, "E4.10.4.4", {"start": v(-53, 46) * mm, "end": v(-53, 56) * mm});
            skLineSegment(sketch, "E4.0.4.5", {"start": v(-53, 9) * mm, "end": v(-63, 9) * mm});
            skPoint(sketch, "E4.3.4.5", {"position": v(-58, 14) * mm});
            skLineSegment(sketch, "E4.4.4.5", {"start": v(-63, 9) * mm, "end": v(-63, 19) * mm});
            skLineSegment(sketch, "E4.7.4.5", {"start": v(-53, 19) * mm, "end": v(-63, 19) * mm});
            skLineSegment(sketch, "E4.10.4.5", {"start": v(-53, 9) * mm, "end": v(-53, 19) * mm});
            skLineSegment(sketch, "E4.0.4.6", {"start": v(-53, -28) * mm, "end": v(-63, -28) * mm});
            skPoint(sketch, "E4.3.4.6", {"position": v(-58, -23) * mm});
            skLineSegment(sketch, "E4.4.4.6", {"start": v(-63, -28) * mm, "end": v(-63, -18) * mm});
            skLineSegment(sketch, "E4.7.4.6", {"start": v(-53, -18) * mm, "end": v(-63, -18) * mm});
            skLineSegment(sketch, "E4.10.4.6", {"start": v(-53, -28) * mm, "end": v(-53, -18) * mm});
            skLineSegment(sketch, "E4.0.4.7", {"start": v(-53, -65) * mm, "end": v(-63, -65) * mm});
            skPoint(sketch, "E4.3.4.7", {"position": v(-58, -60) * mm});
            skLineSegment(sketch, "E4.4.4.7", {"start": v(-63, -65) * mm, "end": v(-63, -55) * mm});
            skLineSegment(sketch, "E4.7.4.7", {"start": v(-53, -55) * mm, "end": v(-63, -55) * mm});
            skLineSegment(sketch, "E4.10.4.7", {"start": v(-53, -65) * mm, "end": v(-53, -55) * mm});
            skLineSegment(sketch, "E4.0.4.8", {"start": v(-53, -102) * mm, "end": v(-63, -102) * mm});
            skPoint(sketch, "E4.3.4.8", {"position": v(-58, -97) * mm});
            skLineSegment(sketch, "E4.4.4.8", {"start": v(-63, -102) * mm, "end": v(-63, -92) * mm});
            skLineSegment(sketch, "E4.7.4.8", {"start": v(-53, -92) * mm, "end": v(-63, -92) * mm});
            skLineSegment(sketch, "E4.10.4.8", {"start": v(-53, -102) * mm, "end": v(-53, -92) * mm});
            skLineSegment(sketch, "E4.0.4.9", {"start": v(-53, -139) * mm, "end": v(-63, -139) * mm});
            skPoint(sketch, "E4.3.4.9", {"position": v(-58, -134) * mm});
            skLineSegment(sketch, "E4.4.4.9", {"start": v(-63, -139) * mm, "end": v(-63, -129) * mm});
            skLineSegment(sketch, "E4.7.4.9", {"start": v(-53, -129) * mm, "end": v(-63, -129) * mm});
            skLineSegment(sketch, "E4.10.4.9", {"start": v(-53, -139) * mm, "end": v(-53, -129) * mm});
            skLineSegment(sketch, "E4.0.4.10", {"start": v(-53, -176) * mm, "end": v(-63, -176) * mm});
            skPoint(sketch, "E4.3.4.10", {"position": v(-58, -171) * mm});
            skLineSegment(sketch, "E4.4.4.10", {"start": v(-63, -176) * mm, "end": v(-63, -166) * mm});
            skLineSegment(sketch, "E4.7.4.10", {"start": v(-53, -166) * mm, "end": v(-63, -166) * mm});
            skLineSegment(sketch, "E4.10.4.10", {"start": v(-53, -176) * mm, "end": v(-53, -166) * mm});
            skLineSegment(sketch, "E4.0.4.11", {"start": v(-53, -213) * mm, "end": v(-63, -213) * mm});
            skPoint(sketch, "E4.3.4.11", {"position": v(-58, -208) * mm});
            skLineSegment(sketch, "E4.4.4.11", {"start": v(-63, -213) * mm, "end": v(-63, -203) * mm});
            skLineSegment(sketch, "E4.7.4.11", {"start": v(-53, -203) * mm, "end": v(-63, -203) * mm});
            skLineSegment(sketch, "E4.10.4.11", {"start": v(-53, -213) * mm, "end": v(-53, -203) * mm});
            skLineSegment(sketch, "E4.0.5.2", {"start": v(-16, 120) * mm, "end": v(-26, 120) * mm});
            skPoint(sketch, "E4.3.5.2", {"position": v(-21, 125) * mm});
            skLineSegment(sketch, "E4.4.5.2", {"start": v(-26, 120) * mm, "end": v(-26, 130) * mm});
            skLineSegment(sketch, "E4.7.5.2", {"start": v(-16, 130) * mm, "end": v(-26, 130) * mm});
            skLineSegment(sketch, "E4.10.5.2", {"start": v(-16, 120) * mm, "end": v(-16, 130) * mm});
            skLineSegment(sketch, "E4.0.5.3", {"start": v(-16, 83) * mm, "end": v(-26, 83) * mm});
            skPoint(sketch, "E4.3.5.3", {"position": v(-21, 88) * mm});
            skLineSegment(sketch, "E4.4.5.3", {"start": v(-26, 83) * mm, "end": v(-26, 93) * mm});
            skLineSegment(sketch, "E4.7.5.3", {"start": v(-16, 93) * mm, "end": v(-26, 93) * mm});
            skLineSegment(sketch, "E4.10.5.3", {"start": v(-16, 83) * mm, "end": v(-16, 93) * mm});
            skLineSegment(sketch, "E4.0.5.4", {"start": v(-16, 46) * mm, "end": v(-26, 46) * mm});
            skPoint(sketch, "E4.3.5.4", {"position": v(-21, 51) * mm});
            skLineSegment(sketch, "E4.4.5.4", {"start": v(-26, 46) * mm, "end": v(-26, 56) * mm});
            skLineSegment(sketch, "E4.7.5.4", {"start": v(-16, 56) * mm, "end": v(-26, 56) * mm});
            skLineSegment(sketch, "E4.10.5.4", {"start": v(-16, 46) * mm, "end": v(-16, 56) * mm});
            skLineSegment(sketch, "E4.0.5.5", {"start": v(-16, 9) * mm, "end": v(-26, 9) * mm});
            skPoint(sketch, "E4.3.5.5", {"position": v(-21, 14) * mm});
            skLineSegment(sketch, "E4.4.5.5", {"start": v(-26, 9) * mm, "end": v(-26, 19) * mm});
            skLineSegment(sketch, "E4.7.5.5", {"start": v(-16, 19) * mm, "end": v(-26, 19) * mm});
            skLineSegment(sketch, "E4.10.5.5", {"start": v(-16, 9) * mm, "end": v(-16, 19) * mm});
            skLineSegment(sketch, "E4.0.5.6", {"start": v(-16, -28) * mm, "end": v(-26, -28) * mm});
            skPoint(sketch, "E4.3.5.6", {"position": v(-21, -23) * mm});
            skLineSegment(sketch, "E4.4.5.6", {"start": v(-26, -28) * mm, "end": v(-26, -18) * mm});
            skLineSegment(sketch, "E4.7.5.6", {"start": v(-16, -18) * mm, "end": v(-26, -18) * mm});
            skLineSegment(sketch, "E4.10.5.6", {"start": v(-16, -28) * mm, "end": v(-16, -18) * mm});
            skLineSegment(sketch, "E4.0.5.7", {"start": v(-16, -65) * mm, "end": v(-26, -65) * mm});
            skPoint(sketch, "E4.3.5.7", {"position": v(-21, -60) * mm});
            skLineSegment(sketch, "E4.4.5.7", {"start": v(-26, -65) * mm, "end": v(-26, -55) * mm});
            skLineSegment(sketch, "E4.7.5.7", {"start": v(-16, -55) * mm, "end": v(-26, -55) * mm});
            skLineSegment(sketch, "E4.10.5.7", {"start": v(-16, -65) * mm, "end": v(-16, -55) * mm});
            skLineSegment(sketch, "E4.0.5.8", {"start": v(-16, -102) * mm, "end": v(-26, -102) * mm});
            skPoint(sketch, "E4.3.5.8", {"position": v(-21, -97) * mm});
            skLineSegment(sketch, "E4.4.5.8", {"start": v(-26, -102) * mm, "end": v(-26, -92) * mm});
            skLineSegment(sketch, "E4.7.5.8", {"start": v(-16, -92) * mm, "end": v(-26, -92) * mm});
            skLineSegment(sketch, "E4.10.5.8", {"start": v(-16, -102) * mm, "end": v(-16, -92) * mm});
            skLineSegment(sketch, "E4.0.5.9", {"start": v(-16, -139) * mm, "end": v(-26, -139) * mm});
            skPoint(sketch, "E4.3.5.9", {"position": v(-21, -134) * mm});
            skLineSegment(sketch, "E4.4.5.9", {"start": v(-26, -139) * mm, "end": v(-26, -129) * mm});
            skLineSegment(sketch, "E4.7.5.9", {"start": v(-16, -129) * mm, "end": v(-26, -129) * mm});
            skLineSegment(sketch, "E4.10.5.9", {"start": v(-16, -139) * mm, "end": v(-16, -129) * mm});
            skLineSegment(sketch, "E4.0.5.10", {"start": v(-16, -176) * mm, "end": v(-26, -176) * mm});
            skPoint(sketch, "E4.3.5.10", {"position": v(-21, -171) * mm});
            skLineSegment(sketch, "E4.4.5.10", {"start": v(-26, -176) * mm, "end": v(-26, -166) * mm});
            skLineSegment(sketch, "E4.7.5.10", {"start": v(-16, -166) * mm, "end": v(-26, -166) * mm});
            skLineSegment(sketch, "E4.10.5.10", {"start": v(-16, -176) * mm, "end": v(-16, -166) * mm});
            skLineSegment(sketch, "E4.0.5.11", {"start": v(-16, -213) * mm, "end": v(-26, -213) * mm});
            skPoint(sketch, "E4.3.5.11", {"position": v(-21, -208) * mm});
            skLineSegment(sketch, "E4.4.5.11", {"start": v(-26, -213) * mm, "end": v(-26, -203) * mm});
            skLineSegment(sketch, "E4.7.5.11", {"start": v(-16, -203) * mm, "end": v(-26, -203) * mm});
            skLineSegment(sketch, "E4.10.5.11", {"start": v(-16, -213) * mm, "end": v(-16, -203) * mm});
            skLineSegment(sketch, "E4.0.6.2", {"start": v(21, 120) * mm, "end": v(11, 120) * mm});
            skPoint(sketch, "E4.3.6.2", {"position": v(16, 125) * mm});
            skLineSegment(sketch, "E4.4.6.2", {"start": v(11, 120) * mm, "end": v(11, 130) * mm});
            skLineSegment(sketch, "E4.7.6.2", {"start": v(21, 130) * mm, "end": v(11, 130) * mm});
            skLineSegment(sketch, "E4.10.6.2", {"start": v(21, 120) * mm, "end": v(21, 130) * mm});
            skLineSegment(sketch, "E4.0.6.3", {"start": v(21, 83) * mm, "end": v(11, 83) * mm});
            skPoint(sketch, "E4.3.6.3", {"position": v(16, 88) * mm});
            skLineSegment(sketch, "E4.4.6.3", {"start": v(11, 83) * mm, "end": v(11, 93) * mm});
            skLineSegment(sketch, "E4.7.6.3", {"start": v(21, 93) * mm, "end": v(11, 93) * mm});
            skLineSegment(sketch, "E4.10.6.3", {"start": v(21, 83) * mm, "end": v(21, 93) * mm});
            skLineSegment(sketch, "E4.0.6.4", {"start": v(21, 46) * mm, "end": v(11, 46) * mm});
            skPoint(sketch, "E4.3.6.4", {"position": v(16, 51) * mm});
            skLineSegment(sketch, "E4.4.6.4", {"start": v(11, 46) * mm, "end": v(11, 56) * mm});
            skLineSegment(sketch, "E4.7.6.4", {"start": v(21, 56) * mm, "end": v(11, 56) * mm});
            skLineSegment(sketch, "E4.10.6.4", {"start": v(21, 46) * mm, "end": v(21, 56) * mm});
            skLineSegment(sketch, "E4.0.6.5", {"start": v(21, 9) * mm, "end": v(11, 9) * mm});
            skPoint(sketch, "E4.3.6.5", {"position": v(16, 14) * mm});
            skLineSegment(sketch, "E4.4.6.5", {"start": v(11, 9) * mm, "end": v(11, 19) * mm});
            skLineSegment(sketch, "E4.7.6.5", {"start": v(21, 19) * mm, "end": v(11, 19) * mm});
            skLineSegment(sketch, "E4.10.6.5", {"start": v(21, 9) * mm, "end": v(21, 19) * mm});
            skLineSegment(sketch, "E4.0.6.6", {"start": v(21, -28) * mm, "end": v(11, -28) * mm});
            skPoint(sketch, "E4.3.6.6", {"position": v(16, -23) * mm});
            skLineSegment(sketch, "E4.4.6.6", {"start": v(11, -28) * mm, "end": v(11, -18) * mm});
            skLineSegment(sketch, "E4.7.6.6", {"start": v(21, -18) * mm, "end": v(11, -18) * mm});
            skLineSegment(sketch, "E4.10.6.6", {"start": v(21, -28) * mm, "end": v(21, -18) * mm});
            skLineSegment(sketch, "E4.0.6.7", {"start": v(21, -65) * mm, "end": v(11, -65) * mm});
            skPoint(sketch, "E4.3.6.7", {"position": v(16, -60) * mm});
            skLineSegment(sketch, "E4.4.6.7", {"start": v(11, -65) * mm, "end": v(11, -55) * mm});
            skLineSegment(sketch, "E4.7.6.7", {"start": v(21, -55) * mm, "end": v(11, -55) * mm});
            skLineSegment(sketch, "E4.10.6.7", {"start": v(21, -65) * mm, "end": v(21, -55) * mm});
            skLineSegment(sketch, "E4.0.6.8", {"start": v(21, -102) * mm, "end": v(11, -102) * mm});
            skPoint(sketch, "E4.3.6.8", {"position": v(16, -97) * mm});
            skLineSegment(sketch, "E4.4.6.8", {"start": v(11, -102) * mm, "end": v(11, -92) * mm});
            skLineSegment(sketch, "E4.7.6.8", {"start": v(21, -92) * mm, "end": v(11, -92) * mm});
            skLineSegment(sketch, "E4.10.6.8", {"start": v(21, -102) * mm, "end": v(21, -92) * mm});
            skLineSegment(sketch, "E4.0.6.9", {"start": v(21, -139) * mm, "end": v(11, -139) * mm});
            skPoint(sketch, "E4.3.6.9", {"position": v(16, -134) * mm});
            skLineSegment(sketch, "E4.4.6.9", {"start": v(11, -139) * mm, "end": v(11, -129) * mm});
            skLineSegment(sketch, "E4.7.6.9", {"start": v(21, -129) * mm, "end": v(11, -129) * mm});
            skLineSegment(sketch, "E4.10.6.9", {"start": v(21, -139) * mm, "end": v(21, -129) * mm});
            skLineSegment(sketch, "E4.0.6.10", {"start": v(21, -176) * mm, "end": v(11, -176) * mm});
            skPoint(sketch, "E4.3.6.10", {"position": v(16, -171) * mm});
            skLineSegment(sketch, "E4.4.6.10", {"start": v(11, -176) * mm, "end": v(11, -166) * mm});
            skLineSegment(sketch, "E4.7.6.10", {"start": v(21, -166) * mm, "end": v(11, -166) * mm});
            skLineSegment(sketch, "E4.10.6.10", {"start": v(21, -176) * mm, "end": v(21, -166) * mm});
            skLineSegment(sketch, "E4.0.6.11", {"start": v(21, -213) * mm, "end": v(11, -213) * mm});
            skPoint(sketch, "E4.3.6.11", {"position": v(16, -208) * mm});
            skLineSegment(sketch, "E4.4.6.11", {"start": v(11, -213) * mm, "end": v(11, -203) * mm});
            skLineSegment(sketch, "E4.7.6.11", {"start": v(21, -203) * mm, "end": v(11, -203) * mm});
            skLineSegment(sketch, "E4.10.6.11", {"start": v(21, -213) * mm, "end": v(21, -203) * mm});
            skLineSegment(sketch, "E4.0.7.2", {"start": v(58, 120) * mm, "end": v(48, 120) * mm});
            skPoint(sketch, "E4.3.7.2", {"position": v(53, 125) * mm});
            skLineSegment(sketch, "E4.4.7.2", {"start": v(48, 120) * mm, "end": v(48, 130) * mm});
            skLineSegment(sketch, "E4.7.7.2", {"start": v(58, 130) * mm, "end": v(48, 130) * mm});
            skLineSegment(sketch, "E4.10.7.2", {"start": v(58, 120) * mm, "end": v(58, 130) * mm});
            skLineSegment(sketch, "E4.0.7.3", {"start": v(58, 83) * mm, "end": v(48, 83) * mm});
            skPoint(sketch, "E4.3.7.3", {"position": v(53, 88) * mm});
            skLineSegment(sketch, "E4.4.7.3", {"start": v(48, 83) * mm, "end": v(48, 93) * mm});
            skLineSegment(sketch, "E4.7.7.3", {"start": v(58, 93) * mm, "end": v(48, 93) * mm});
            skLineSegment(sketch, "E4.10.7.3", {"start": v(58, 83) * mm, "end": v(58, 93) * mm});
            skLineSegment(sketch, "E4.0.7.4", {"start": v(58, 46) * mm, "end": v(48, 46) * mm});
            skPoint(sketch, "E4.3.7.4", {"position": v(53, 51) * mm});
            skLineSegment(sketch, "E4.4.7.4", {"start": v(48, 46) * mm, "end": v(48, 56) * mm});
            skLineSegment(sketch, "E4.7.7.4", {"start": v(58, 56) * mm, "end": v(48, 56) * mm});
            skLineSegment(sketch, "E4.10.7.4", {"start": v(58, 46) * mm, "end": v(58, 56) * mm});
            skLineSegment(sketch, "E4.0.7.5", {"start": v(58, 9) * mm, "end": v(48, 9) * mm});
            skPoint(sketch, "E4.3.7.5", {"position": v(53, 14) * mm});
            skLineSegment(sketch, "E4.4.7.5", {"start": v(48, 9) * mm, "end": v(48, 19) * mm});
            skLineSegment(sketch, "E4.7.7.5", {"start": v(58, 19) * mm, "end": v(48, 19) * mm});
            skLineSegment(sketch, "E4.10.7.5", {"start": v(58, 9) * mm, "end": v(58, 19) * mm});
            skLineSegment(sketch, "E4.0.7.6", {"start": v(58, -28) * mm, "end": v(48, -28) * mm});
            skPoint(sketch, "E4.3.7.6", {"position": v(53, -23) * mm});
            skLineSegment(sketch, "E4.4.7.6", {"start": v(48, -28) * mm, "end": v(48, -18) * mm});
            skLineSegment(sketch, "E4.7.7.6", {"start": v(58, -18) * mm, "end": v(48, -18) * mm});
            skLineSegment(sketch, "E4.10.7.6", {"start": v(58, -28) * mm, "end": v(58, -18) * mm});
            skLineSegment(sketch, "E4.0.7.7", {"start": v(58, -65) * mm, "end": v(48, -65) * mm});
            skPoint(sketch, "E4.3.7.7", {"position": v(53, -60) * mm});
            skLineSegment(sketch, "E4.4.7.7", {"start": v(48, -65) * mm, "end": v(48, -55) * mm});
            skLineSegment(sketch, "E4.7.7.7", {"start": v(58, -55) * mm, "end": v(48, -55) * mm});
            skLineSegment(sketch, "E4.10.7.7", {"start": v(58, -65) * mm, "end": v(58, -55) * mm});
            skLineSegment(sketch, "E4.0.7.8", {"start": v(58, -102) * mm, "end": v(48, -102) * mm});
            skPoint(sketch, "E4.3.7.8", {"position": v(53, -97) * mm});
            skLineSegment(sketch, "E4.4.7.8", {"start": v(48, -102) * mm, "end": v(48, -92) * mm});
            skLineSegment(sketch, "E4.7.7.8", {"start": v(58, -92) * mm, "end": v(48, -92) * mm});
            skLineSegment(sketch, "E4.10.7.8", {"start": v(58, -102) * mm, "end": v(58, -92) * mm});
            skLineSegment(sketch, "E4.0.7.9", {"start": v(58, -139) * mm, "end": v(48, -139) * mm});
            skPoint(sketch, "E4.3.7.9", {"position": v(53, -134) * mm});
            skLineSegment(sketch, "E4.4.7.9", {"start": v(48, -139) * mm, "end": v(48, -129) * mm});
            skLineSegment(sketch, "E4.7.7.9", {"start": v(58, -129) * mm, "end": v(48, -129) * mm});
            skLineSegment(sketch, "E4.10.7.9", {"start": v(58, -139) * mm, "end": v(58, -129) * mm});
            skLineSegment(sketch, "E4.0.7.10", {"start": v(58, -176) * mm, "end": v(48, -176) * mm});
            skPoint(sketch, "E4.3.7.10", {"position": v(53, -171) * mm});
            skLineSegment(sketch, "E4.4.7.10", {"start": v(48, -176) * mm, "end": v(48, -166) * mm});
            skLineSegment(sketch, "E4.7.7.10", {"start": v(58, -166) * mm, "end": v(48, -166) * mm});
            skLineSegment(sketch, "E4.10.7.10", {"start": v(58, -176) * mm, "end": v(58, -166) * mm});
            skLineSegment(sketch, "E4.0.7.11", {"start": v(58, -213) * mm, "end": v(48, -213) * mm});
            skPoint(sketch, "E4.3.7.11", {"position": v(53, -208) * mm});
            skLineSegment(sketch, "E4.4.7.11", {"start": v(48, -213) * mm, "end": v(48, -203) * mm});
            skLineSegment(sketch, "E4.7.7.11", {"start": v(58, -203) * mm, "end": v(48, -203) * mm});
            skLineSegment(sketch, "E4.10.7.11", {"start": v(58, -213) * mm, "end": v(58, -203) * mm});
            skLineSegment(sketch, "E4.0.8.2", {"start": v(95, 120) * mm, "end": v(85, 120) * mm});
            skPoint(sketch, "E4.3.8.2", {"position": v(90, 125) * mm});
            skLineSegment(sketch, "E4.4.8.2", {"start": v(85, 120) * mm, "end": v(85, 130) * mm});
            skLineSegment(sketch, "E4.7.8.2", {"start": v(95, 130) * mm, "end": v(85, 130) * mm});
            skLineSegment(sketch, "E4.10.8.2", {"start": v(95, 120) * mm, "end": v(95, 130) * mm});
            skLineSegment(sketch, "E4.0.8.3", {"start": v(95, 83) * mm, "end": v(85, 83) * mm});
            skPoint(sketch, "E4.3.8.3", {"position": v(90, 88) * mm});
            skLineSegment(sketch, "E4.4.8.3", {"start": v(85, 83) * mm, "end": v(85, 93) * mm});
            skLineSegment(sketch, "E4.7.8.3", {"start": v(95, 93) * mm, "end": v(85, 93) * mm});
            skLineSegment(sketch, "E4.10.8.3", {"start": v(95, 83) * mm, "end": v(95, 93) * mm});
            skLineSegment(sketch, "E4.0.8.4", {"start": v(95, 46) * mm, "end": v(85, 46) * mm});
            skPoint(sketch, "E4.3.8.4", {"position": v(90, 51) * mm});
            skLineSegment(sketch, "E4.4.8.4", {"start": v(85, 46) * mm, "end": v(85, 56) * mm});
            skLineSegment(sketch, "E4.7.8.4", {"start": v(95, 56) * mm, "end": v(85, 56) * mm});
            skLineSegment(sketch, "E4.10.8.4", {"start": v(95, 46) * mm, "end": v(95, 56) * mm});
            skLineSegment(sketch, "E4.0.8.5", {"start": v(95, 9) * mm, "end": v(85, 9) * mm});
            skPoint(sketch, "E4.3.8.5", {"position": v(90, 14) * mm});
            skLineSegment(sketch, "E4.4.8.5", {"start": v(85, 9) * mm, "end": v(85, 19) * mm});
            skLineSegment(sketch, "E4.7.8.5", {"start": v(95, 19) * mm, "end": v(85, 19) * mm});
            skLineSegment(sketch, "E4.10.8.5", {"start": v(95, 9) * mm, "end": v(95, 19) * mm});
            skLineSegment(sketch, "E4.0.8.6", {"start": v(95, -28) * mm, "end": v(85, -28) * mm});
            skPoint(sketch, "E4.3.8.6", {"position": v(90, -23) * mm});
            skLineSegment(sketch, "E4.4.8.6", {"start": v(85, -28) * mm, "end": v(85, -18) * mm});
            skLineSegment(sketch, "E4.7.8.6", {"start": v(95, -18) * mm, "end": v(85, -18) * mm});
            skLineSegment(sketch, "E4.10.8.6", {"start": v(95, -28) * mm, "end": v(95, -18) * mm});
            skLineSegment(sketch, "E4.0.8.7", {"start": v(95, -65) * mm, "end": v(85, -65) * mm});
            skPoint(sketch, "E4.3.8.7", {"position": v(90, -60) * mm});
            skLineSegment(sketch, "E4.4.8.7", {"start": v(85, -65) * mm, "end": v(85, -55) * mm});
            skLineSegment(sketch, "E4.7.8.7", {"start": v(95, -55) * mm, "end": v(85, -55) * mm});
            skLineSegment(sketch, "E4.10.8.7", {"start": v(95, -65) * mm, "end": v(95, -55) * mm});
            skLineSegment(sketch, "E4.0.8.8", {"start": v(95, -102) * mm, "end": v(85, -102) * mm});
            skPoint(sketch, "E4.3.8.8", {"position": v(90, -97) * mm});
            skLineSegment(sketch, "E4.4.8.8", {"start": v(85, -102) * mm, "end": v(85, -92) * mm});
            skLineSegment(sketch, "E4.7.8.8", {"start": v(95, -92) * mm, "end": v(85, -92) * mm});
            skLineSegment(sketch, "E4.10.8.8", {"start": v(95, -102) * mm, "end": v(95, -92) * mm});
            skLineSegment(sketch, "E4.0.8.9", {"start": v(95, -139) * mm, "end": v(85, -139) * mm});
            skPoint(sketch, "E4.3.8.9", {"position": v(90, -134) * mm});
            skLineSegment(sketch, "E4.4.8.9", {"start": v(85, -139) * mm, "end": v(85, -129) * mm});
            skLineSegment(sketch, "E4.7.8.9", {"start": v(95, -129) * mm, "end": v(85, -129) * mm});
            skLineSegment(sketch, "E4.10.8.9", {"start": v(95, -139) * mm, "end": v(95, -129) * mm});
            skLineSegment(sketch, "E4.0.8.10", {"start": v(95, -176) * mm, "end": v(85, -176) * mm});
            skPoint(sketch, "E4.3.8.10", {"position": v(90, -171) * mm});
            skLineSegment(sketch, "E4.4.8.10", {"start": v(85, -176) * mm, "end": v(85, -166) * mm});
            skLineSegment(sketch, "E4.7.8.10", {"start": v(95, -166) * mm, "end": v(85, -166) * mm});
            skLineSegment(sketch, "E4.10.8.10", {"start": v(95, -176) * mm, "end": v(95, -166) * mm});
            skLineSegment(sketch, "E4.0.8.11", {"start": v(95, -213) * mm, "end": v(85, -213) * mm});
            skPoint(sketch, "E4.3.8.11", {"position": v(90, -208) * mm});
            skLineSegment(sketch, "E4.4.8.11", {"start": v(85, -213) * mm, "end": v(85, -203) * mm});
            skLineSegment(sketch, "E4.7.8.11", {"start": v(95, -203) * mm, "end": v(85, -203) * mm});
            skLineSegment(sketch, "E4.10.8.11", {"start": v(95, -213) * mm, "end": v(95, -203) * mm});
            skLineSegment(sketch, "E4.0.9.2", {"start": v(132, 120) * mm, "end": v(122, 120) * mm});
            skPoint(sketch, "E4.3.9.2", {"position": v(127, 125) * mm});
            skLineSegment(sketch, "E4.4.9.2", {"start": v(122, 120) * mm, "end": v(122, 130) * mm});
            skLineSegment(sketch, "E4.7.9.2", {"start": v(132, 130) * mm, "end": v(122, 130) * mm});
            skLineSegment(sketch, "E4.10.9.2", {"start": v(132, 120) * mm, "end": v(132, 130) * mm});
            skLineSegment(sketch, "E4.0.9.3", {"start": v(132, 83) * mm, "end": v(122, 83) * mm});
            skPoint(sketch, "E4.3.9.3", {"position": v(127, 88) * mm});
            skLineSegment(sketch, "E4.4.9.3", {"start": v(122, 83) * mm, "end": v(122, 93) * mm});
            skLineSegment(sketch, "E4.7.9.3", {"start": v(132, 93) * mm, "end": v(122, 93) * mm});
            skLineSegment(sketch, "E4.10.9.3", {"start": v(132, 83) * mm, "end": v(132, 93) * mm});
            skLineSegment(sketch, "E4.0.9.4", {"start": v(132, 46) * mm, "end": v(122, 46) * mm});
            skPoint(sketch, "E4.3.9.4", {"position": v(127, 51) * mm});
            skLineSegment(sketch, "E4.4.9.4", {"start": v(122, 46) * mm, "end": v(122, 56) * mm});
            skLineSegment(sketch, "E4.7.9.4", {"start": v(132, 56) * mm, "end": v(122, 56) * mm});
            skLineSegment(sketch, "E4.10.9.4", {"start": v(132, 46) * mm, "end": v(132, 56) * mm});
            skLineSegment(sketch, "E4.0.9.5", {"start": v(132, 9) * mm, "end": v(122, 9) * mm});
            skPoint(sketch, "E4.3.9.5", {"position": v(127, 14) * mm});
            skLineSegment(sketch, "E4.4.9.5", {"start": v(122, 9) * mm, "end": v(122, 19) * mm});
            skLineSegment(sketch, "E4.7.9.5", {"start": v(132, 19) * mm, "end": v(122, 19) * mm});
            skLineSegment(sketch, "E4.10.9.5", {"start": v(132, 9) * mm, "end": v(132, 19) * mm});
            skLineSegment(sketch, "E4.0.9.6", {"start": v(132, -28) * mm, "end": v(122, -28) * mm});
            skPoint(sketch, "E4.3.9.6", {"position": v(127, -23) * mm});
            skLineSegment(sketch, "E4.4.9.6", {"start": v(122, -28) * mm, "end": v(122, -18) * mm});
            skLineSegment(sketch, "E4.7.9.6", {"start": v(132, -18) * mm, "end": v(122, -18) * mm});
            skLineSegment(sketch, "E4.10.9.6", {"start": v(132, -28) * mm, "end": v(132, -18) * mm});
            skLineSegment(sketch, "E4.0.9.7", {"start": v(132, -65) * mm, "end": v(122, -65) * mm});
            skPoint(sketch, "E4.3.9.7", {"position": v(127, -60) * mm});
            skLineSegment(sketch, "E4.4.9.7", {"start": v(122, -65) * mm, "end": v(122, -55) * mm});
            skLineSegment(sketch, "E4.7.9.7", {"start": v(132, -55) * mm, "end": v(122, -55) * mm});
            skLineSegment(sketch, "E4.10.9.7", {"start": v(132, -65) * mm, "end": v(132, -55) * mm});
            skLineSegment(sketch, "E4.0.9.8", {"start": v(132, -102) * mm, "end": v(122, -102) * mm});
            skPoint(sketch, "E4.3.9.8", {"position": v(127, -97) * mm});
            skLineSegment(sketch, "E4.4.9.8", {"start": v(122, -102) * mm, "end": v(122, -92) * mm});
            skLineSegment(sketch, "E4.7.9.8", {"start": v(132, -92) * mm, "end": v(122, -92) * mm});
            skLineSegment(sketch, "E4.10.9.8", {"start": v(132, -102) * mm, "end": v(132, -92) * mm});
            skLineSegment(sketch, "E4.0.9.9", {"start": v(132, -139) * mm, "end": v(122, -139) * mm});
            skPoint(sketch, "E4.3.9.9", {"position": v(127, -134) * mm});
            skLineSegment(sketch, "E4.4.9.9", {"start": v(122, -139) * mm, "end": v(122, -129) * mm});
            skLineSegment(sketch, "E4.7.9.9", {"start": v(132, -129) * mm, "end": v(122, -129) * mm});
            skLineSegment(sketch, "E4.10.9.9", {"start": v(132, -139) * mm, "end": v(132, -129) * mm});
            skLineSegment(sketch, "E4.0.9.10", {"start": v(132, -176) * mm, "end": v(122, -176) * mm});
            skPoint(sketch, "E4.3.9.10", {"position": v(127, -171) * mm});
            skLineSegment(sketch, "E4.4.9.10", {"start": v(122, -176) * mm, "end": v(122, -166) * mm});
            skLineSegment(sketch, "E4.7.9.10", {"start": v(132, -166) * mm, "end": v(122, -166) * mm});
            skLineSegment(sketch, "E4.10.9.10", {"start": v(132, -176) * mm, "end": v(132, -166) * mm});
            skLineSegment(sketch, "E4.0.9.11", {"start": v(132, -213) * mm, "end": v(122, -213) * mm});
            skPoint(sketch, "E4.3.9.11", {"position": v(127, -208) * mm});
            skLineSegment(sketch, "E4.4.9.11", {"start": v(122, -213) * mm, "end": v(122, -203) * mm});
            skLineSegment(sketch, "E4.7.9.11", {"start": v(132, -203) * mm, "end": v(122, -203) * mm});
            skLineSegment(sketch, "E4.10.9.11", {"start": v(132, -213) * mm, "end": v(132, -203) * mm});
            skLineSegment(sketch, "E4.0.10.2", {"start": v(169, 120) * mm, "end": v(159, 120) * mm});
            skPoint(sketch, "E4.3.10.2", {"position": v(164, 125) * mm});
            skLineSegment(sketch, "E4.4.10.2", {"start": v(159, 120) * mm, "end": v(159, 130) * mm});
            skLineSegment(sketch, "E4.7.10.2", {"start": v(169, 130) * mm, "end": v(159, 130) * mm});
            skLineSegment(sketch, "E4.10.10.2", {"start": v(169, 120) * mm, "end": v(169, 130) * mm});
            skLineSegment(sketch, "E4.0.10.3", {"start": v(169, 83) * mm, "end": v(159, 83) * mm});
            skPoint(sketch, "E4.3.10.3", {"position": v(164, 88) * mm});
            skLineSegment(sketch, "E4.4.10.3", {"start": v(159, 83) * mm, "end": v(159, 93) * mm});
            skLineSegment(sketch, "E4.7.10.3", {"start": v(169, 93) * mm, "end": v(159, 93) * mm});
            skLineSegment(sketch, "E4.10.10.3", {"start": v(169, 83) * mm, "end": v(169, 93) * mm});
            skLineSegment(sketch, "E4.0.10.4", {"start": v(169, 46) * mm, "end": v(159, 46) * mm});
            skPoint(sketch, "E4.3.10.4", {"position": v(164, 51) * mm});
            skLineSegment(sketch, "E4.4.10.4", {"start": v(159, 46) * mm, "end": v(159, 56) * mm});
            skLineSegment(sketch, "E4.7.10.4", {"start": v(169, 56) * mm, "end": v(159, 56) * mm});
            skLineSegment(sketch, "E4.10.10.4", {"start": v(169, 46) * mm, "end": v(169, 56) * mm});
            skLineSegment(sketch, "E4.0.10.5", {"start": v(169, 9) * mm, "end": v(159, 9) * mm});
            skPoint(sketch, "E4.3.10.5", {"position": v(164, 14) * mm});
            skLineSegment(sketch, "E4.4.10.5", {"start": v(159, 9) * mm, "end": v(159, 19) * mm});
            skLineSegment(sketch, "E4.7.10.5", {"start": v(169, 19) * mm, "end": v(159, 19) * mm});
            skLineSegment(sketch, "E4.10.10.5", {"start": v(169, 9) * mm, "end": v(169, 19) * mm});
            skLineSegment(sketch, "E4.0.10.6", {"start": v(169, -28) * mm, "end": v(159, -28) * mm});
            skPoint(sketch, "E4.3.10.6", {"position": v(164, -23) * mm});
            skLineSegment(sketch, "E4.4.10.6", {"start": v(159, -28) * mm, "end": v(159, -18) * mm});
            skLineSegment(sketch, "E4.7.10.6", {"start": v(169, -18) * mm, "end": v(159, -18) * mm});
            skLineSegment(sketch, "E4.10.10.6", {"start": v(169, -28) * mm, "end": v(169, -18) * mm});
            skLineSegment(sketch, "E4.0.10.7", {"start": v(169, -65) * mm, "end": v(159, -65) * mm});
            skPoint(sketch, "E4.3.10.7", {"position": v(164, -60) * mm});
            skLineSegment(sketch, "E4.4.10.7", {"start": v(159, -65) * mm, "end": v(159, -55) * mm});
            skLineSegment(sketch, "E4.7.10.7", {"start": v(169, -55) * mm, "end": v(159, -55) * mm});
            skLineSegment(sketch, "E4.10.10.7", {"start": v(169, -65) * mm, "end": v(169, -55) * mm});
            skLineSegment(sketch, "E4.0.10.8", {"start": v(169, -102) * mm, "end": v(159, -102) * mm});
            skPoint(sketch, "E4.3.10.8", {"position": v(164, -97) * mm});
            skLineSegment(sketch, "E4.4.10.8", {"start": v(159, -102) * mm, "end": v(159, -92) * mm});
            skLineSegment(sketch, "E4.7.10.8", {"start": v(169, -92) * mm, "end": v(159, -92) * mm});
            skLineSegment(sketch, "E4.10.10.8", {"start": v(169, -102) * mm, "end": v(169, -92) * mm});
            skLineSegment(sketch, "E4.0.10.9", {"start": v(169, -139) * mm, "end": v(159, -139) * mm});
            skPoint(sketch, "E4.3.10.9", {"position": v(164, -134) * mm});
            skLineSegment(sketch, "E4.4.10.9", {"start": v(159, -139) * mm, "end": v(159, -129) * mm});
            skLineSegment(sketch, "E4.7.10.9", {"start": v(169, -129) * mm, "end": v(159, -129) * mm});
            skLineSegment(sketch, "E4.10.10.9", {"start": v(169, -139) * mm, "end": v(169, -129) * mm});
            skLineSegment(sketch, "E4.0.10.10", {"start": v(169, -176) * mm, "end": v(159, -176) * mm});
            skPoint(sketch, "E4.3.10.10", {"position": v(164, -171) * mm});
            skLineSegment(sketch, "E4.4.10.10", {"start": v(159, -176) * mm, "end": v(159, -166) * mm});
            skLineSegment(sketch, "E4.7.10.10", {"start": v(169, -166) * mm, "end": v(159, -166) * mm});
            skLineSegment(sketch, "E4.10.10.10", {"start": v(169, -176) * mm, "end": v(169, -166) * mm});
            skLineSegment(sketch, "E4.0.10.11", {"start": v(169, -213) * mm, "end": v(159, -213) * mm});
            skPoint(sketch, "E4.3.10.11", {"position": v(164, -208) * mm});
            skLineSegment(sketch, "E4.4.10.11", {"start": v(159, -213) * mm, "end": v(159, -203) * mm});
            skLineSegment(sketch, "E4.7.10.11", {"start": v(169, -203) * mm, "end": v(159, -203) * mm});
            skLineSegment(sketch, "E4.10.10.11", {"start": v(169, -213) * mm, "end": v(169, -203) * mm});
            skLineSegment(sketch, "E4.0.11.2", {"start": v(206, 120) * mm, "end": v(196, 120) * mm});
            skPoint(sketch, "E4.3.11.2", {"position": v(201, 125) * mm});
            skLineSegment(sketch, "E4.4.11.2", {"start": v(196, 120) * mm, "end": v(196, 130) * mm});
            skLineSegment(sketch, "E4.7.11.2", {"start": v(206, 130) * mm, "end": v(196, 130) * mm});
            skLineSegment(sketch, "E4.10.11.2", {"start": v(206, 120) * mm, "end": v(206, 130) * mm});
            skLineSegment(sketch, "E4.0.11.3", {"start": v(206, 83) * mm, "end": v(196, 83) * mm});
            skPoint(sketch, "E4.3.11.3", {"position": v(201, 88) * mm});
            skLineSegment(sketch, "E4.4.11.3", {"start": v(196, 83) * mm, "end": v(196, 93) * mm});
            skLineSegment(sketch, "E4.7.11.3", {"start": v(206, 93) * mm, "end": v(196, 93) * mm});
            skLineSegment(sketch, "E4.10.11.3", {"start": v(206, 83) * mm, "end": v(206, 93) * mm});
            skLineSegment(sketch, "E4.0.11.4", {"start": v(206, 46) * mm, "end": v(196, 46) * mm});
            skPoint(sketch, "E4.3.11.4", {"position": v(201, 51) * mm});
            skLineSegment(sketch, "E4.4.11.4", {"start": v(196, 46) * mm, "end": v(196, 56) * mm});
            skLineSegment(sketch, "E4.7.11.4", {"start": v(206, 56) * mm, "end": v(196, 56) * mm});
            skLineSegment(sketch, "E4.10.11.4", {"start": v(206, 46) * mm, "end": v(206, 56) * mm});
            skLineSegment(sketch, "E4.0.11.5", {"start": v(206, 9) * mm, "end": v(196, 9) * mm});
            skPoint(sketch, "E4.3.11.5", {"position": v(201, 14) * mm});
            skLineSegment(sketch, "E4.4.11.5", {"start": v(196, 9) * mm, "end": v(196, 19) * mm});
            skLineSegment(sketch, "E4.7.11.5", {"start": v(206, 19) * mm, "end": v(196, 19) * mm});
            skLineSegment(sketch, "E4.10.11.5", {"start": v(206, 9) * mm, "end": v(206, 19) * mm});
            skLineSegment(sketch, "E4.0.11.6", {"start": v(206, -28) * mm, "end": v(196, -28) * mm});
            skPoint(sketch, "E4.3.11.6", {"position": v(201, -23) * mm});
            skLineSegment(sketch, "E4.4.11.6", {"start": v(196, -28) * mm, "end": v(196, -18) * mm});
            skLineSegment(sketch, "E4.7.11.6", {"start": v(206, -18) * mm, "end": v(196, -18) * mm});
            skLineSegment(sketch, "E4.10.11.6", {"start": v(206, -28) * mm, "end": v(206, -18) * mm});
            skLineSegment(sketch, "E4.0.11.7", {"start": v(206, -65) * mm, "end": v(196, -65) * mm});
            skPoint(sketch, "E4.3.11.7", {"position": v(201, -60) * mm});
            skLineSegment(sketch, "E4.4.11.7", {"start": v(196, -65) * mm, "end": v(196, -55) * mm});
            skLineSegment(sketch, "E4.7.11.7", {"start": v(206, -55) * mm, "end": v(196, -55) * mm});
            skLineSegment(sketch, "E4.10.11.7", {"start": v(206, -65) * mm, "end": v(206, -55) * mm});
            skLineSegment(sketch, "E4.0.11.8", {"start": v(206, -102) * mm, "end": v(196, -102) * mm});
            skPoint(sketch, "E4.3.11.8", {"position": v(201, -97) * mm});
            skLineSegment(sketch, "E4.4.11.8", {"start": v(196, -102) * mm, "end": v(196, -92) * mm});
            skLineSegment(sketch, "E4.7.11.8", {"start": v(206, -92) * mm, "end": v(196, -92) * mm});
            skLineSegment(sketch, "E4.10.11.8", {"start": v(206, -102) * mm, "end": v(206, -92) * mm});
            skLineSegment(sketch, "E4.0.11.9", {"start": v(206, -139) * mm, "end": v(196, -139) * mm});
            skPoint(sketch, "E4.3.11.9", {"position": v(201, -134) * mm});
            skLineSegment(sketch, "E4.4.11.9", {"start": v(196, -139) * mm, "end": v(196, -129) * mm});
            skLineSegment(sketch, "E4.7.11.9", {"start": v(206, -129) * mm, "end": v(196, -129) * mm});
            skLineSegment(sketch, "E4.10.11.9", {"start": v(206, -139) * mm, "end": v(206, -129) * mm});
            skLineSegment(sketch, "E4.0.11.10", {"start": v(206, -176) * mm, "end": v(196, -176) * mm});
            skPoint(sketch, "E4.3.11.10", {"position": v(201, -171) * mm});
            skLineSegment(sketch, "E4.4.11.10", {"start": v(196, -176) * mm, "end": v(196, -166) * mm});
            skLineSegment(sketch, "E4.7.11.10", {"start": v(206, -166) * mm, "end": v(196, -166) * mm});
            skLineSegment(sketch, "E4.10.11.10", {"start": v(206, -176) * mm, "end": v(206, -166) * mm});
            skLineSegment(sketch, "E4.0.11.11", {"start": v(206, -213) * mm, "end": v(196, -213) * mm});
            skPoint(sketch, "E4.3.11.11", {"position": v(201, -208) * mm});
            skLineSegment(sketch, "E4.4.11.11", {"start": v(196, -213) * mm, "end": v(196, -203) * mm});
            skLineSegment(sketch, "E4.7.11.11", {"start": v(206, -203) * mm, "end": v(196, -203) * mm});
            skLineSegment(sketch, "E4.10.11.11", {"start": v(206, -213) * mm, "end": v(206, -203) * mm});
            skSolve(sketch);
        }
        {
            var Q0;
            Q0=makeQuery(id+"F4.imprint","IMPRINT",FACE,{"disambiguationData":[TD([[makeQuery(id+"F4.imprint","IMPRINT",EDGE,{"derivedFrom":sQuery(id+"F4.wireOp",EDGE,"E2.bottom")}),-1.0]])]});
            var Q1;
            Q1=makeQuery(id+"F4.imprint","IMPRINT",FACE,{"disambiguationData":[TD([[makeQuery(id+"F4.imprint","IMPRINT",EDGE,{"derivedFrom":sQuery(id+"F4.wireOp",EDGE,"E3.1.0.0")}),-1.0]])]});
            var Q2;
            Q2=makeQuery(id+"F4.imprint","IMPRINT",FACE,{"disambiguationData":[TD([[makeQuery(id+"F4.imprint","IMPRINT",EDGE,{"derivedFrom":sQuery(id+"F4.wireOp",EDGE,"E3.2.0.0")}),-1.0]])]});
            var Q3;
            Q3=makeQuery(id+"F4.imprint","IMPRINT",FACE,{"disambiguationData":[TD([[makeQuery(id+"F4.imprint","IMPRINT",EDGE,{"derivedFrom":sQuery(id+"F4.wireOp",EDGE,"E3.3.0.0")}),-1.0]])]});
            var Q4;
            Q4=makeQuery(id+"F4.imprint","IMPRINT",FACE,{"disambiguationData":[TD([[makeQuery(id+"F4.imprint","IMPRINT",EDGE,{"derivedFrom":sQuery(id+"F4.wireOp",EDGE,"E3.4.0.0")}),-1.0]])]});
            var Q5;
            Q5=makeQuery(id+"F4.imprint","IMPRINT",FACE,{"disambiguationData":[TD([[makeQuery(id+"F4.imprint","IMPRINT",EDGE,{"derivedFrom":sQuery(id+"F4.wireOp",EDGE,"E4.0.2.10")}),-1.0]])]});
            var Q6;
            Q6=makeQuery(id+"F4.imprint","IMPRINT",FACE,{"disambiguationData":[TD([[makeQuery(id+"F4.imprint","IMPRINT",EDGE,{"derivedFrom":sQuery(id+"F4.wireOp",EDGE,"E4.0.2.8")}),-1.0]])]});
            var Q7;
            Q7=makeQuery(id+"F4.imprint","IMPRINT",FACE,{"disambiguationData":[TD([[makeQuery(id+"F4.imprint","IMPRINT",EDGE,{"derivedFrom":sQuery(id+"F4.wireOp",EDGE,"E4.0.1.9")}),-1.0]])]});
            var Q8;
            Q8=makeQuery(id+"F4.imprint","IMPRINT",FACE,{"disambiguationData":[TD([[makeQuery(id+"F4.imprint","IMPRINT",EDGE,{"derivedFrom":sQuery(id+"F4.wireOp",EDGE,"E4.0.3.9")}),-1.0]])]});
            var Q9;
            Q9=makeQuery(id+"F4.imprint","IMPRINT",FACE,{"disambiguationData":[TD([[makeQuery(id+"F4.imprint","IMPRINT",EDGE,{"derivedFrom":sQuery(id+"F4.wireOp",EDGE,"E4.0.1.8")}),-1.0]])]});
            var Q10;
            Q10=makeQuery(id+"F4.imprint","IMPRINT",FACE,{"disambiguationData":[TD([[makeQuery(id+"F4.imprint","IMPRINT",EDGE,{"derivedFrom":sQuery(id+"F4.wireOp",EDGE,"E4.0.2.9")}),-1.0]])]});
            var Q11;
            Q11=makeQuery(id+"F4.imprint","IMPRINT",FACE,{"disambiguationData":[TD([[makeQuery(id+"F4.imprint","IMPRINT",EDGE,{"derivedFrom":sQuery(id+"F4.wireOp",EDGE,"E4.0.4.8")}),-1.0]])]});
            var Q12;
            Q12=makeQuery(id+"F4.imprint","IMPRINT",FACE,{"disambiguationData":[TD([[makeQuery(id+"F4.imprint","IMPRINT",EDGE,{"derivedFrom":sQuery(id+"F4.wireOp",EDGE,"E4.0.1.10")}),-1.0]])]});
            var Q13;
            Q13=makeQuery(id+"F4.imprint","IMPRINT",FACE,{"disambiguationData":[TD([[makeQuery(id+"F4.imprint","IMPRINT",EDGE,{"derivedFrom":sQuery(id+"F4.wireOp",EDGE,"E4.0.4.7")}),-1.0]])]});
            var Q14;
            Q14=makeQuery(id+"F4.imprint","IMPRINT",FACE,{"disambiguationData":[TD([[makeQuery(id+"F4.imprint","IMPRINT",EDGE,{"derivedFrom":sQuery(id+"F4.wireOp",EDGE,"E4.0.3.7")}),-1.0]])]});
            var Q15;
            Q15=makeQuery(id+"F4.imprint","IMPRINT",FACE,{"disambiguationData":[TD([[makeQuery(id+"F4.imprint","IMPRINT",EDGE,{"derivedFrom":sQuery(id+"F4.wireOp",EDGE,"E4.0.3.8")}),-1.0]])]});
            var Q16;
            Q16=makeQuery(id+"F4.imprint","IMPRINT",FACE,{"disambiguationData":[TD([[makeQuery(id+"F4.imprint","IMPRINT",EDGE,{"derivedFrom":sQuery(id+"F4.wireOp",EDGE,"E4.0.4.9")}),-1.0]])]});
            var Q17;
            Q17=makeQuery(id+"F4.imprint","IMPRINT",FACE,{"disambiguationData":[TD([[makeQuery(id+"F4.imprint","IMPRINT",EDGE,{"derivedFrom":sQuery(id+"F4.wireOp",EDGE,"E4.0.3.10")}),-1.0]])]});
            var Q18;
            Q18=makeQuery(id+"F4.imprint","IMPRINT",FACE,{"disambiguationData":[TD([[makeQuery(id+"F4.imprint","IMPRINT",EDGE,{"derivedFrom":sQuery(id+"F4.wireOp",EDGE,"E4.0.8.10")}),-1.0]])]});
            var Q19;
            Q19=makeQuery(id+"F4.imprint","IMPRINT",FACE,{"disambiguationData":[TD([[makeQuery(id+"F4.imprint","IMPRINT",EDGE,{"derivedFrom":sQuery(id+"F4.wireOp",EDGE,"E4.0.3.6")}),-1.0]])]});
            var Q20;
            Q20=makeQuery(id+"F4.imprint","IMPRINT",FACE,{"disambiguationData":[TD([[makeQuery(id+"F4.imprint","IMPRINT",EDGE,{"derivedFrom":sQuery(id+"F4.wireOp",EDGE,"E4.0.6.3")}),-1.0]])]});
            var Q21;
            Q21=makeQuery(id+"F4.imprint","IMPRINT",FACE,{"disambiguationData":[TD([[makeQuery(id+"F4.imprint","IMPRINT",EDGE,{"derivedFrom":sQuery(id+"F4.wireOp",EDGE,"E4.0.3.3")}),-1.0]])]});
            var Q22;
            Q22=makeQuery(id+"F4.imprint","IMPRINT",FACE,{"disambiguationData":[TD([[makeQuery(id+"F4.imprint","IMPRINT",EDGE,{"derivedFrom":sQuery(id+"F4.wireOp",EDGE,"E4.0.0.3")}),-1.0]])]});
            var Q23;
            Q23=makeQuery(id+"F4.imprint","IMPRINT",FACE,{"disambiguationData":[TD([[makeQuery(id+"F4.imprint","IMPRINT",EDGE,{"derivedFrom":sQuery(id+"F4.wireOp",EDGE,"E4.0.10.10")}),-1.0]])]});
            var Q24;
            Q24=makeQuery(id+"F4.imprint","IMPRINT",FACE,{"disambiguationData":[TD([[makeQuery(id+"F4.imprint","IMPRINT",EDGE,{"derivedFrom":sQuery(id+"F4.wireOp",EDGE,"E4.0.8.9")}),-1.0]])]});
            var Q25;
            Q25=makeQuery(id+"F4.imprint","IMPRINT",FACE,{"disambiguationData":[TD([[makeQuery(id+"F4.imprint","IMPRINT",EDGE,{"derivedFrom":sQuery(id+"F4.wireOp",EDGE,"E4.0.4.10")}),-1.0]])]});
            var Q26;
            Q26=makeQuery(id+"F4.imprint","IMPRINT",FACE,{"disambiguationData":[TD([[makeQuery(id+"F4.imprint","IMPRINT",EDGE,{"derivedFrom":sQuery(id+"F4.wireOp",EDGE,"E4.0.7.3")}),-1.0]])]});
            var Q27;
            Q27=makeQuery(id+"F4.imprint","IMPRINT",FACE,{"disambiguationData":[TD([[makeQuery(id+"F4.imprint","IMPRINT",EDGE,{"derivedFrom":sQuery(id+"F4.wireOp",EDGE,"E4.0.3.2")}),-1.0]])]});
            var Q28;
            Q28=makeQuery(id+"F4.imprint","IMPRINT",FACE,{"disambiguationData":[TD([[makeQuery(id+"F4.imprint","IMPRINT",EDGE,{"derivedFrom":sQuery(id+"F4.wireOp",EDGE,"E4.0.7.10")}),-1.0]])]});
            var Q29;
            Q29=makeQuery(id+"F4.imprint","IMPRINT",FACE,{"disambiguationData":[TD([[makeQuery(id+"F4.imprint","IMPRINT",EDGE,{"derivedFrom":sQuery(id+"F4.wireOp",EDGE,"E4.0.8.3")}),-1.0]])]});
            var Q30;
            Q30=makeQuery(id+"F4.imprint","IMPRINT",FACE,{"disambiguationData":[TD([[makeQuery(id+"F4.imprint","IMPRINT",EDGE,{"derivedFrom":sQuery(id+"F4.wireOp",EDGE,"E4.0.11.10")}),-1.0]])]});
            var Q31;
            Q31=makeQuery(id+"F4.imprint","IMPRINT",FACE,{"disambiguationData":[TD([[makeQuery(id+"F4.imprint","IMPRINT",EDGE,{"derivedFrom":sQuery(id+"F4.wireOp",EDGE,"E4.0.3.5")}),-1.0]])]});
            var Q32;
            Q32=makeQuery(id+"F4.imprint","IMPRINT",FACE,{"disambiguationData":[TD([[makeQuery(id+"F4.imprint","IMPRINT",EDGE,{"derivedFrom":sQuery(id+"F4.wireOp",EDGE,"E4.0.8.4")}),-1.0]])]});
            var Q33;
            Q33=makeQuery(id+"F4.imprint","IMPRINT",FACE,{"disambiguationData":[TD([[makeQuery(id+"F4.imprint","IMPRINT",EDGE,{"derivedFrom":sQuery(id+"F4.wireOp",EDGE,"E4.0.3.4")}),-1.0]])]});
            var Q34;
            Q34=makeQuery(id+"F4.imprint","IMPRINT",FACE,{"disambiguationData":[TD([[makeQuery(id+"F4.imprint","IMPRINT",EDGE,{"derivedFrom":sQuery(id+"F4.wireOp",EDGE,"E3.8.0.0")}),-1.0]])]});
            var Q35;
            Q35=makeQuery(id+"F4.imprint","IMPRINT",FACE,{"disambiguationData":[TD([[makeQuery(id+"F4.imprint","IMPRINT",EDGE,{"derivedFrom":sQuery(id+"F4.wireOp",EDGE,"E4.0.8.8")}),-1.0]])]});
            var Q36;
            Q36=makeQuery(id+"F4.imprint","IMPRINT",FACE,{"disambiguationData":[TD([[makeQuery(id+"F4.imprint","IMPRINT",EDGE,{"derivedFrom":sQuery(id+"F4.wireOp",EDGE,"E4.0.3.11")}),-1.0]])]});
            var Q37;
            Q37=makeQuery(id+"F4.imprint","IMPRINT",FACE,{"disambiguationData":[TD([[makeQuery(id+"F4.imprint","IMPRINT",EDGE,{"derivedFrom":sQuery(id+"F4.wireOp",EDGE,"E4.0.4.3")}),-1.0]])]});
            var Q38;
            Q38=makeQuery(id+"F4.imprint","IMPRINT",FACE,{"disambiguationData":[TD([[makeQuery(id+"F4.imprint","IMPRINT",EDGE,{"derivedFrom":sQuery(id+"F4.wireOp",EDGE,"E4.0.8.7")}),-1.0]])]});
            var Q39;
            Q39=makeQuery(id+"F4.imprint","IMPRINT",FACE,{"disambiguationData":[TD([[makeQuery(id+"F4.imprint","IMPRINT",EDGE,{"derivedFrom":sQuery(id+"F4.wireOp",EDGE,"E4.0.9.10")}),-1.0]])]});
            var Q40;
            Q40=makeQuery(id+"F4.imprint","IMPRINT",FACE,{"disambiguationData":[TD([[makeQuery(id+"F4.imprint","IMPRINT",EDGE,{"derivedFrom":sQuery(id+"F4.wireOp",EDGE,"E4.0.9.3")}),-1.0]])]});
            var Q41;
            Q41=makeQuery(id+"F4.imprint","IMPRINT",FACE,{"disambiguationData":[TD([[makeQuery(id+"F4.imprint","IMPRINT",EDGE,{"derivedFrom":sQuery(id+"F4.wireOp",EDGE,"E4.0.0.10")}),-1.0]])]});
            var Q42;
            Q42=makeQuery(id+"F4.imprint","IMPRINT",FACE,{"disambiguationData":[TD([[makeQuery(id+"F4.imprint","IMPRINT",EDGE,{"derivedFrom":sQuery(id+"F4.wireOp",EDGE,"E4.0.8.11")}),-1.0]])]});
            var Q43;
            Q43=makeQuery(id+"F4.imprint","IMPRINT",FACE,{"disambiguationData":[TD([[makeQuery(id+"F4.imprint","IMPRINT",EDGE,{"derivedFrom":sQuery(id+"F4.wireOp",EDGE,"E4.0.10.3")}),-1.0]])]});
            var Q44;
            Q44=makeQuery(id+"F4.imprint","IMPRINT",FACE,{"disambiguationData":[TD([[makeQuery(id+"F4.imprint","IMPRINT",EDGE,{"derivedFrom":sQuery(id+"F4.wireOp",EDGE,"E4.0.5.3")}),-1.0]])]});
            var Q45;
            Q45=makeQuery(id+"F4.imprint","IMPRINT",FACE,{"disambiguationData":[TD([[makeQuery(id+"F4.imprint","IMPRINT",EDGE,{"derivedFrom":sQuery(id+"F4.wireOp",EDGE,"E4.0.8.6")}),-1.0]])]});
            var Q46;
            Q46=makeQuery(id+"F4.imprint","IMPRINT",FACE,{"disambiguationData":[TD([[makeQuery(id+"F4.imprint","IMPRINT",EDGE,{"derivedFrom":sQuery(id+"F4.wireOp",EDGE,"E4.0.1.3")}),-1.0]])]});
            var Q47;
            Q47=makeQuery(id+"F4.imprint","IMPRINT",FACE,{"disambiguationData":[TD([[makeQuery(id+"F4.imprint","IMPRINT",EDGE,{"derivedFrom":sQuery(id+"F4.wireOp",EDGE,"E4.0.8.5")}),-1.0]])]});
            var Q48;
            Q48=makeQuery(id+"F4.imprint","IMPRINT",FACE,{"disambiguationData":[TD([[makeQuery(id+"F4.imprint","IMPRINT",EDGE,{"derivedFrom":sQuery(id+"F4.wireOp",EDGE,"E4.0.6.10")}),-1.0]])]});
            var Q49;
            Q49=makeQuery(id+"F4.imprint","IMPRINT",FACE,{"disambiguationData":[TD([[makeQuery(id+"F4.imprint","IMPRINT",EDGE,{"derivedFrom":sQuery(id+"F4.wireOp",EDGE,"E4.0.2.3")}),-1.0]])]});
            var Q50;
            Q50=makeQuery(id+"F4.imprint","IMPRINT",FACE,{"disambiguationData":[TD([[makeQuery(id+"F4.imprint","IMPRINT",EDGE,{"derivedFrom":sQuery(id+"F4.wireOp",EDGE,"E3.3.1.0")}),-1.0]])]});
            var Q51;
            Q51=makeQuery(id+"F4.imprint","IMPRINT",FACE,{"disambiguationData":[TD([[makeQuery(id+"F4.imprint","IMPRINT",EDGE,{"derivedFrom":sQuery(id+"F4.wireOp",EDGE,"E4.0.11.3")}),-1.0]])]});
            var Q52;
            Q52=makeQuery(id+"F4.imprint","IMPRINT",FACE,{"disambiguationData":[TD([[makeQuery(id+"F4.imprint","IMPRINT",EDGE,{"derivedFrom":sQuery(id+"F4.wireOp",EDGE,"E4.0.8.2")}),-1.0]])]});
            var Q53;
            Q53=makeQuery(id+"F4.imprint","IMPRINT",FACE,{"disambiguationData":[TD([[makeQuery(id+"F4.imprint","IMPRINT",EDGE,{"derivedFrom":sQuery(id+"F4.wireOp",EDGE,"E4.0.5.10")}),-1.0]])]});
            var Q54;
            Q54=makeQuery(id+"F4.imprint","IMPRINT",FACE,{"disambiguationData":[TD([[makeQuery(id+"F4.imprint","IMPRINT",EDGE,{"derivedFrom":sQuery(id+"F4.wireOp",EDGE,"E3.8.1.0")}),-1.0]])]});
            var Q55;
            Q55=makeQuery(id+"F4.imprint","IMPRINT",FACE,{"disambiguationData":[TD([[makeQuery(id+"F4.imprint","IMPRINT",EDGE,{"derivedFrom":sQuery(id+"F4.wireOp",EDGE,"E4.0.7.4")}),-1.0]])]});
            var Q56;
            Q56=makeQuery(id+"F4.imprint","IMPRINT",FACE,{"disambiguationData":[TD([[makeQuery(id+"F4.imprint","IMPRINT",EDGE,{"derivedFrom":sQuery(id+"F4.wireOp",EDGE,"E4.0.9.2")}),-1.0]])]});
            var Q57;
            Q57=makeQuery(id+"F4.imprint","IMPRINT",FACE,{"disambiguationData":[TD([[makeQuery(id+"F4.imprint","IMPRINT",EDGE,{"derivedFrom":sQuery(id+"F4.wireOp",EDGE,"E4.0.11.8")}),-1.0]])]});
            var Q58;
            Q58=makeQuery(id+"F4.imprint","IMPRINT",FACE,{"disambiguationData":[TD([[makeQuery(id+"F4.imprint","IMPRINT",EDGE,{"derivedFrom":sQuery(id+"F4.wireOp",EDGE,"E4.0.0.5")}),-1.0]])]});
            var Q59;
            Q59=makeQuery(id+"F4.imprint","IMPRINT",FACE,{"disambiguationData":[TD([[makeQuery(id+"F4.imprint","IMPRINT",EDGE,{"derivedFrom":sQuery(id+"F4.wireOp",EDGE,"E4.0.1.2")}),-1.0]])]});
            var Q60;
            Q60=makeQuery(id+"F4.imprint","IMPRINT",FACE,{"disambiguationData":[TD([[makeQuery(id+"F4.imprint","IMPRINT",EDGE,{"derivedFrom":sQuery(id+"F4.wireOp",EDGE,"E3.9.0.0")}),-1.0]])]});
            var Q61;
            Q61=makeQuery(id+"F4.imprint","IMPRINT",FACE,{"disambiguationData":[TD([[makeQuery(id+"F4.imprint","IMPRINT",EDGE,{"derivedFrom":sQuery(id+"F4.wireOp",EDGE,"E3.9.1.0")}),-1.0]])]});
            var Q62;
            Q62=makeQuery(id+"F4.imprint","IMPRINT",FACE,{"disambiguationData":[TD([[makeQuery(id+"F4.imprint","IMPRINT",EDGE,{"derivedFrom":sQuery(id+"F4.wireOp",EDGE,"E4.0.11.6")}),-1.0]])]});
            var Q63;
            Q63=makeQuery(id+"F4.imprint","IMPRINT",FACE,{"disambiguationData":[TD([[makeQuery(id+"F4.imprint","IMPRINT",EDGE,{"derivedFrom":sQuery(id+"F4.wireOp",EDGE,"E3.7.1.0")}),-1.0]])]});
            var Q64;
            Q64=makeQuery(id+"F4.imprint","IMPRINT",FACE,{"disambiguationData":[TD([[makeQuery(id+"F4.imprint","IMPRINT",EDGE,{"derivedFrom":sQuery(id+"F4.wireOp",EDGE,"E4.0.0.11")}),-1.0]])]});
            var Q65;
            Q65=makeQuery(id+"F4.imprint","IMPRINT",FACE,{"disambiguationData":[TD([[makeQuery(id+"F4.imprint","IMPRINT",EDGE,{"derivedFrom":sQuery(id+"F4.wireOp",EDGE,"E4.0.11.5")}),-1.0]])]});
            var Q66;
            Q66=makeQuery(id+"F4.imprint","IMPRINT",FACE,{"disambiguationData":[TD([[makeQuery(id+"F4.imprint","IMPRINT",EDGE,{"derivedFrom":sQuery(id+"F4.wireOp",EDGE,"E3.11.1.0")}),-1.0]])]});
            var Q67;
            Q67=makeQuery(id+"F4.imprint","IMPRINT",FACE,{"disambiguationData":[TD([[makeQuery(id+"F4.imprint","IMPRINT",EDGE,{"derivedFrom":sQuery(id+"F4.wireOp",EDGE,"E4.0.6.8")}),-1.0]])]});
            var Q68;
            Q68=makeQuery(id+"F4.imprint","IMPRINT",FACE,{"disambiguationData":[TD([[makeQuery(id+"F4.imprint","IMPRINT",EDGE,{"derivedFrom":sQuery(id+"F4.wireOp",EDGE,"E4.0.10.4")}),-1.0]])]});
            var Q69;
            Q69=makeQuery(id+"F4.imprint","IMPRINT",FACE,{"disambiguationData":[TD([[makeQuery(id+"F4.imprint","IMPRINT",EDGE,{"derivedFrom":sQuery(id+"F4.wireOp",EDGE,"E3.11.0.0")}),-1.0]])]});
            var Q70;
            Q70=makeQuery(id+"F4.imprint","IMPRINT",FACE,{"disambiguationData":[TD([[makeQuery(id+"F4.imprint","IMPRINT",EDGE,{"derivedFrom":sQuery(id+"F4.wireOp",EDGE,"E4.0.2.11")}),-1.0]])]});
            var Q71;
            Q71=makeQuery(id+"F4.imprint","IMPRINT",FACE,{"disambiguationData":[TD([[makeQuery(id+"F4.imprint","IMPRINT",EDGE,{"derivedFrom":sQuery(id+"F4.wireOp",EDGE,"E4.0.2.5")}),-1.0]])]});
            var Q72;
            Q72=makeQuery(id+"F4.imprint","IMPRINT",FACE,{"disambiguationData":[TD([[makeQuery(id+"F4.imprint","IMPRINT",EDGE,{"derivedFrom":sQuery(id+"F4.wireOp",EDGE,"E4.0.5.5")}),-1.0]])]});
            var Q73;
            Q73=makeQuery(id+"F4.imprint","IMPRINT",FACE,{"disambiguationData":[TD([[makeQuery(id+"F4.imprint","IMPRINT",EDGE,{"derivedFrom":sQuery(id+"F4.wireOp",EDGE,"E4.0.4.2")}),-1.0]])]});
            var Q74;
            Q74=makeQuery(id+"F4.imprint","IMPRINT",FACE,{"disambiguationData":[TD([[makeQuery(id+"F4.imprint","IMPRINT",EDGE,{"derivedFrom":sQuery(id+"F4.wireOp",EDGE,"E4.0.9.4")}),-1.0]])]});
            var Q75;
            Q75=makeQuery(id+"F4.imprint","IMPRINT",FACE,{"disambiguationData":[TD([[makeQuery(id+"F4.imprint","IMPRINT",EDGE,{"derivedFrom":sQuery(id+"F4.wireOp",EDGE,"E3.10.0.0")}),-1.0]])]});
            var Q76;
            Q76=makeQuery(id+"F4.imprint","IMPRINT",FACE,{"disambiguationData":[TD([[makeQuery(id+"F4.imprint","IMPRINT",EDGE,{"derivedFrom":sQuery(id+"F4.wireOp",EDGE,"E3.5.1.0")}),-1.0]])]});
            var Q77;
            Q77=makeQuery(id+"F4.imprint","IMPRINT",FACE,{"disambiguationData":[TD([[makeQuery(id+"F4.imprint","IMPRINT",EDGE,{"derivedFrom":sQuery(id+"F4.wireOp",EDGE,"E4.0.0.8")}),-1.0]])]});
            var Q78;
            Q78=makeQuery(id+"F4.imprint","IMPRINT",FACE,{"disambiguationData":[TD([[makeQuery(id+"F4.imprint","IMPRINT",EDGE,{"derivedFrom":sQuery(id+"F4.wireOp",EDGE,"E4.0.10.5")}),-1.0]])]});
            var Q79;
            Q79=makeQuery(id+"F4.imprint","IMPRINT",FACE,{"disambiguationData":[TD([[makeQuery(id+"F4.imprint","IMPRINT",EDGE,{"derivedFrom":sQuery(id+"F4.wireOp",EDGE,"E4.0.10.9")}),-1.0]])]});
            var Q80;
            Q80=makeQuery(id+"F4.imprint","IMPRINT",FACE,{"disambiguationData":[TD([[makeQuery(id+"F4.imprint","IMPRINT",EDGE,{"derivedFrom":sQuery(id+"F4.wireOp",EDGE,"E4.0.4.5")}),-1.0]])]});
            var Q81;
            Q81=makeQuery(id+"F4.imprint","IMPRINT",FACE,{"disambiguationData":[TD([[makeQuery(id+"F4.imprint","IMPRINT",EDGE,{"derivedFrom":sQuery(id+"F4.wireOp",EDGE,"E4.0.7.11")}),-1.0]])]});
            var Q82;
            Q82=makeQuery(id+"F4.imprint","IMPRINT",FACE,{"disambiguationData":[TD([[makeQuery(id+"F4.imprint","IMPRINT",EDGE,{"derivedFrom":sQuery(id+"F4.wireOp",EDGE,"E3.5.0.0")}),-1.0]])]});
            var Q83;
            Q83=makeQuery(id+"F4.imprint","IMPRINT",FACE,{"disambiguationData":[TD([[makeQuery(id+"F4.imprint","IMPRINT",EDGE,{"derivedFrom":sQuery(id+"F4.wireOp",EDGE,"E3.4.1.0")}),-1.0]])]});
            var Q84;
            Q84=makeQuery(id+"F4.imprint","IMPRINT",FACE,{"disambiguationData":[TD([[makeQuery(id+"F4.imprint","IMPRINT",EDGE,{"derivedFrom":sQuery(id+"F4.wireOp",EDGE,"E4.0.10.11")}),-1.0]])]});
            var Q85;
            Q85=makeQuery(id+"F4.imprint","IMPRINT",FACE,{"disambiguationData":[TD([[makeQuery(id+"F4.imprint","IMPRINT",EDGE,{"derivedFrom":sQuery(id+"F4.wireOp",EDGE,"E4.0.5.7")}),-1.0]])]});
            var Q86;
            Q86=makeQuery(id+"F4.imprint","IMPRINT",FACE,{"disambiguationData":[TD([[makeQuery(id+"F4.imprint","IMPRINT",EDGE,{"derivedFrom":sQuery(id+"F4.wireOp",EDGE,"E4.0.10.8")}),-1.0]])]});
            var Q87;
            Q87=makeQuery(id+"F4.imprint","IMPRINT",FACE,{"disambiguationData":[TD([[makeQuery(id+"F4.imprint","IMPRINT",EDGE,{"derivedFrom":sQuery(id+"F4.wireOp",EDGE,"E4.0.1.6")}),-1.0]])]});
            var Q88;
            Q88=makeQuery(id+"F4.imprint","IMPRINT",FACE,{"disambiguationData":[TD([[makeQuery(id+"F4.imprint","IMPRINT",EDGE,{"derivedFrom":sQuery(id+"F4.wireOp",EDGE,"E3.6.0.0")}),-1.0]])]});
            var Q89;
            Q89=makeQuery(id+"F4.imprint","IMPRINT",FACE,{"disambiguationData":[TD([[makeQuery(id+"F4.imprint","IMPRINT",EDGE,{"derivedFrom":sQuery(id+"F4.wireOp",EDGE,"E4.0.4.11")}),-1.0]])]});
            var Q90;
            Q90=makeQuery(id+"F4.imprint","IMPRINT",FACE,{"disambiguationData":[TD([[makeQuery(id+"F4.imprint","IMPRINT",EDGE,{"derivedFrom":sQuery(id+"F4.wireOp",EDGE,"E4.0.9.8")}),-1.0]])]});
            var Q91;
            Q91=makeQuery(id+"F4.imprint","IMPRINT",FACE,{"disambiguationData":[TD([[makeQuery(id+"F4.imprint","IMPRINT",EDGE,{"derivedFrom":sQuery(id+"F4.wireOp",EDGE,"E4.0.7.9")}),-1.0]])]});
            var Q92;
            Q92=makeQuery(id+"F4.imprint","IMPRINT",FACE,{"disambiguationData":[TD([[makeQuery(id+"F4.imprint","IMPRINT",EDGE,{"derivedFrom":sQuery(id+"F4.wireOp",EDGE,"E4.0.9.7")}),-1.0]])]});
            var Q93;
            Q93=makeQuery(id+"F4.imprint","IMPRINT",FACE,{"disambiguationData":[TD([[makeQuery(id+"F4.imprint","IMPRINT",EDGE,{"derivedFrom":sQuery(id+"F4.wireOp",EDGE,"E4.0.11.11")}),-1.0]])]});
            var Q94;
            Q94=makeQuery(id+"F4.imprint","IMPRINT",FACE,{"disambiguationData":[TD([[makeQuery(id+"F4.imprint","IMPRINT",EDGE,{"derivedFrom":sQuery(id+"F4.wireOp",EDGE,"E4.0.11.9")}),-1.0]])]});
            var Q95;
            Q95=makeQuery(id+"F4.imprint","IMPRINT",FACE,{"disambiguationData":[TD([[makeQuery(id+"F4.imprint","IMPRINT",EDGE,{"derivedFrom":sQuery(id+"F4.wireOp",EDGE,"E4.0.0.9")}),-1.0]])]});
            var Q96;
            Q96=makeQuery(id+"F4.imprint","IMPRINT",FACE,{"disambiguationData":[TD([[makeQuery(id+"F4.imprint","IMPRINT",EDGE,{"derivedFrom":sQuery(id+"F4.wireOp",EDGE,"E4.0.6.11")}),-1.0]])]});
            var Q97;
            Q97=makeQuery(id+"F4.imprint","IMPRINT",FACE,{"disambiguationData":[TD([[makeQuery(id+"F4.imprint","IMPRINT",EDGE,{"derivedFrom":sQuery(id+"F4.wireOp",EDGE,"E4.0.2.2")}),-1.0]])]});
            var Q98;
            Q98=makeQuery(id+"F4.imprint","IMPRINT",FACE,{"disambiguationData":[TD([[makeQuery(id+"F4.imprint","IMPRINT",EDGE,{"derivedFrom":sQuery(id+"F4.wireOp",EDGE,"E4.0.5.6")}),-1.0]])]});
            var Q99;
            Q99=makeQuery(id+"F4.imprint","IMPRINT",FACE,{"disambiguationData":[TD([[makeQuery(id+"F4.imprint","IMPRINT",EDGE,{"derivedFrom":sQuery(id+"F4.wireOp",EDGE,"E4.0.4.4")}),-1.0]])]});
            var Q100;
            Q100=makeQuery(id+"F4.imprint","IMPRINT",FACE,{"disambiguationData":[TD([[makeQuery(id+"F4.imprint","IMPRINT",EDGE,{"derivedFrom":sQuery(id+"F4.wireOp",EDGE,"E4.0.6.2")}),-1.0]])]});
            var Q101;
            Q101=makeQuery(id+"F4.imprint","IMPRINT",FACE,{"disambiguationData":[TD([[makeQuery(id+"F4.imprint","IMPRINT",EDGE,{"derivedFrom":sQuery(id+"F4.wireOp",EDGE,"E4.0.1.4")}),-1.0]])]});
            var Q102;
            Q102=makeQuery(id+"F4.imprint","IMPRINT",FACE,{"disambiguationData":[TD([[makeQuery(id+"F4.imprint","IMPRINT",EDGE,{"derivedFrom":sQuery(id+"F4.wireOp",EDGE,"E4.0.6.7")}),-1.0]])]});
            var Q103;
            Q103=makeQuery(id+"F4.imprint","IMPRINT",FACE,{"disambiguationData":[TD([[makeQuery(id+"F4.imprint","IMPRINT",EDGE,{"derivedFrom":sQuery(id+"F4.wireOp",EDGE,"E4.0.6.6")}),-1.0]])]});
            var Q104;
            Q104=makeQuery(id+"F4.imprint","IMPRINT",FACE,{"disambiguationData":[TD([[makeQuery(id+"F4.imprint","IMPRINT",EDGE,{"derivedFrom":sQuery(id+"F4.wireOp",EDGE,"E4.0.6.5")}),-1.0]])]});
            var Q105;
            Q105=makeQuery(id+"F4.imprint","IMPRINT",FACE,{"disambiguationData":[TD([[makeQuery(id+"F4.imprint","IMPRINT",EDGE,{"derivedFrom":sQuery(id+"F4.wireOp",EDGE,"E4.0.6.4")}),-1.0]])]});
            var Q106;
            Q106=makeQuery(id+"F4.imprint","IMPRINT",FACE,{"disambiguationData":[TD([[makeQuery(id+"F4.imprint","IMPRINT",EDGE,{"derivedFrom":sQuery(id+"F4.wireOp",EDGE,"E4.0.2.4")}),-1.0]])]});
            var Q107;
            Q107=makeQuery(id+"F4.imprint","IMPRINT",FACE,{"disambiguationData":[TD([[makeQuery(id+"F4.imprint","IMPRINT",EDGE,{"derivedFrom":sQuery(id+"F4.wireOp",EDGE,"E3.6.1.0")}),-1.0]])]});
            var Q108;
            Q108=makeQuery(id+"F4.imprint","IMPRINT",FACE,{"disambiguationData":[TD([[makeQuery(id+"F4.imprint","IMPRINT",EDGE,{"derivedFrom":sQuery(id+"F4.wireOp",EDGE,"E4.0.5.9")}),-1.0]])]});
            var Q109;
            Q109=makeQuery(id+"F4.imprint","IMPRINT",FACE,{"disambiguationData":[TD([[makeQuery(id+"F4.imprint","IMPRINT",EDGE,{"derivedFrom":sQuery(id+"F4.wireOp",EDGE,"E4.0.2.7")}),-1.0]])]});
            var Q110;
            Q110=makeQuery(id+"F4.imprint","IMPRINT",FACE,{"disambiguationData":[TD([[makeQuery(id+"F4.imprint","IMPRINT",EDGE,{"derivedFrom":sQuery(id+"F4.wireOp",EDGE,"E4.0.10.6")}),-1.0]])]});
            var Q111;
            Q111=makeQuery(id+"F4.imprint","IMPRINT",FACE,{"disambiguationData":[TD([[makeQuery(id+"F4.imprint","IMPRINT",EDGE,{"derivedFrom":sQuery(id+"F4.wireOp",EDGE,"E4.0.9.5")}),-1.0]])]});
            var Q112;
            Q112=makeQuery(id+"F4.imprint","IMPRINT",FACE,{"disambiguationData":[TD([[makeQuery(id+"F4.imprint","IMPRINT",EDGE,{"derivedFrom":sQuery(id+"F4.wireOp",EDGE,"E4.0.11.4")}),-1.0]])]});
            var Q113;
            Q113=makeQuery(id+"F4.imprint","IMPRINT",FACE,{"disambiguationData":[TD([[makeQuery(id+"F4.imprint","IMPRINT",EDGE,{"derivedFrom":sQuery(id+"F4.wireOp",EDGE,"E4.0.7.5")}),-1.0]])]});
            var Q114;
            Q114=makeQuery(id+"F4.imprint","IMPRINT",FACE,{"disambiguationData":[TD([[makeQuery(id+"F4.imprint","IMPRINT",EDGE,{"derivedFrom":sQuery(id+"F4.wireOp",EDGE,"E4.0.5.11")}),-1.0]])]});
            var Q115;
            Q115=makeQuery(id+"F4.imprint","IMPRINT",FACE,{"disambiguationData":[TD([[makeQuery(id+"F4.imprint","IMPRINT",EDGE,{"derivedFrom":sQuery(id+"F4.wireOp",EDGE,"E3.10.1.0")}),-1.0]])]});
            var Q116;
            Q116=makeQuery(id+"F4.imprint","IMPRINT",FACE,{"disambiguationData":[TD([[makeQuery(id+"F4.imprint","IMPRINT",EDGE,{"derivedFrom":sQuery(id+"F4.wireOp",EDGE,"E4.0.1.5")}),-1.0]])]});
            var Q117;
            Q117=makeQuery(id+"F4.imprint","IMPRINT",FACE,{"disambiguationData":[TD([[makeQuery(id+"F4.imprint","IMPRINT",EDGE,{"derivedFrom":sQuery(id+"F4.wireOp",EDGE,"E4.0.1.7")}),-1.0]])]});
            var Q118;
            Q118=makeQuery(id+"F4.imprint","IMPRINT",FACE,{"disambiguationData":[TD([[makeQuery(id+"F4.imprint","IMPRINT",EDGE,{"derivedFrom":sQuery(id+"F4.wireOp",EDGE,"E4.0.5.8")}),-1.0]])]});
            var Q119;
            Q119=makeQuery(id+"F4.imprint","IMPRINT",FACE,{"disambiguationData":[TD([[makeQuery(id+"F4.imprint","IMPRINT",EDGE,{"derivedFrom":sQuery(id+"F4.wireOp",EDGE,"E4.0.9.11")}),-1.0]])]});
            var Q120;
            Q120=makeQuery(id+"F4.imprint","IMPRINT",FACE,{"disambiguationData":[TD([[makeQuery(id+"F4.imprint","IMPRINT",EDGE,{"derivedFrom":sQuery(id+"F4.wireOp",EDGE,"E4.0.9.6")}),-1.0]])]});
            var Q121;
            Q121=makeQuery(id+"F4.imprint","IMPRINT",FACE,{"disambiguationData":[TD([[makeQuery(id+"F4.imprint","IMPRINT",EDGE,{"derivedFrom":sQuery(id+"F4.wireOp",EDGE,"E3.2.1.0")}),-1.0]])]});
            var Q122;
            Q122=makeQuery(id+"F4.imprint","IMPRINT",FACE,{"disambiguationData":[TD([[makeQuery(id+"F4.imprint","IMPRINT",EDGE,{"derivedFrom":sQuery(id+"F4.wireOp",EDGE,"E4.0.0.7")}),-1.0]])]});
            var Q123;
            Q123=makeQuery(id+"F4.imprint","IMPRINT",FACE,{"disambiguationData":[TD([[makeQuery(id+"F4.imprint","IMPRINT",EDGE,{"derivedFrom":sQuery(id+"F4.wireOp",EDGE,"E4.0.0.6")}),-1.0]])]});
            var Q124;
            Q124=makeQuery(id+"F4.imprint","IMPRINT",FACE,{"disambiguationData":[TD([[makeQuery(id+"F4.imprint","IMPRINT",EDGE,{"derivedFrom":sQuery(id+"F4.wireOp",EDGE,"E4.0.1.11")}),-1.0]])]});
            var Q125;
            Q125=makeQuery(id+"F4.imprint","IMPRINT",FACE,{"disambiguationData":[TD([[makeQuery(id+"F4.imprint","IMPRINT",EDGE,{"derivedFrom":sQuery(id+"F4.wireOp",EDGE,"E4.0.6.9")}),-1.0]])]});
            var Q126;
            Q126=makeQuery(id+"F4.imprint","IMPRINT",FACE,{"disambiguationData":[TD([[makeQuery(id+"F4.imprint","IMPRINT",EDGE,{"derivedFrom":sQuery(id+"F4.wireOp",EDGE,"E4.0.5.4")}),-1.0]])]});
            var Q127;
            Q127=makeQuery(id+"F4.imprint","IMPRINT",FACE,{"disambiguationData":[TD([[makeQuery(id+"F4.imprint","IMPRINT",EDGE,{"derivedFrom":sQuery(id+"F4.wireOp",EDGE,"E3.7.0.0")}),-1.0]])]});
            var Q128;
            Q128=makeQuery(id+"F4.imprint","IMPRINT",FACE,{"disambiguationData":[TD([[makeQuery(id+"F4.imprint","IMPRINT",EDGE,{"derivedFrom":sQuery(id+"F4.wireOp",EDGE,"E4.0.7.2")}),-1.0]])]});
            var Q129;
            Q129=makeQuery(id+"F4.imprint","IMPRINT",FACE,{"disambiguationData":[TD([[makeQuery(id+"F4.imprint","IMPRINT",EDGE,{"derivedFrom":sQuery(id+"F4.wireOp",EDGE,"E3.1.1.0")}),-1.0]])]});
            var Q130;
            Q130=makeQuery(id+"F4.imprint","IMPRINT",FACE,{"disambiguationData":[TD([[makeQuery(id+"F4.imprint","IMPRINT",EDGE,{"derivedFrom":sQuery(id+"F4.wireOp",EDGE,"E4.0.10.2")}),-1.0]])]});
            var Q131;
            Q131=makeQuery(id+"F4.imprint","IMPRINT",FACE,{"disambiguationData":[TD([[makeQuery(id+"F4.imprint","IMPRINT",EDGE,{"derivedFrom":sQuery(id+"F4.wireOp",EDGE,"E3.0.1.0")}),-1.0]])]});
            var Q132;
            Q132=makeQuery(id+"F4.imprint","IMPRINT",FACE,{"disambiguationData":[TD([[makeQuery(id+"F4.imprint","IMPRINT",EDGE,{"derivedFrom":sQuery(id+"F4.wireOp",EDGE,"E4.0.2.6")}),-1.0]])]});
            var Q133;
            Q133=makeQuery(id+"F4.imprint","IMPRINT",FACE,{"disambiguationData":[TD([[makeQuery(id+"F4.imprint","IMPRINT",EDGE,{"derivedFrom":sQuery(id+"F4.wireOp",EDGE,"E4.0.7.6")}),-1.0]])]});
            var Q134;
            Q134=makeQuery(id+"F4.imprint","IMPRINT",FACE,{"disambiguationData":[TD([[makeQuery(id+"F4.imprint","IMPRINT",EDGE,{"derivedFrom":sQuery(id+"F4.wireOp",EDGE,"E4.0.11.2")}),-1.0]])]});
            var Q135;
            Q135=makeQuery(id+"F4.imprint","IMPRINT",FACE,{"disambiguationData":[TD([[makeQuery(id+"F4.imprint","IMPRINT",EDGE,{"derivedFrom":sQuery(id+"F4.wireOp",EDGE,"E4.0.7.8")}),-1.0]])]});
            var Q136;
            Q136=makeQuery(id+"F4.imprint","IMPRINT",FACE,{"disambiguationData":[TD([[makeQuery(id+"F4.imprint","IMPRINT",EDGE,{"derivedFrom":sQuery(id+"F4.wireOp",EDGE,"E4.0.5.2")}),-1.0]])]});
            var Q137;
            Q137=makeQuery(id+"F4.imprint","IMPRINT",FACE,{"disambiguationData":[TD([[makeQuery(id+"F4.imprint","IMPRINT",EDGE,{"derivedFrom":sQuery(id+"F4.wireOp",EDGE,"E4.0.4.6")}),-1.0]])]});
            var Q138;
            Q138=makeQuery(id+"F4.imprint","IMPRINT",FACE,{"disambiguationData":[TD([[makeQuery(id+"F4.imprint","IMPRINT",EDGE,{"derivedFrom":sQuery(id+"F4.wireOp",EDGE,"E4.0.0.4")}),-1.0]])]});
            var Q139;
            Q139=makeQuery(id+"F4.imprint","IMPRINT",FACE,{"disambiguationData":[TD([[makeQuery(id+"F4.imprint","IMPRINT",EDGE,{"derivedFrom":sQuery(id+"F4.wireOp",EDGE,"E4.0.9.9")}),-1.0]])]});
            var Q140;
            Q140=makeQuery(id+"F4.imprint","IMPRINT",FACE,{"disambiguationData":[TD([[makeQuery(id+"F4.imprint","IMPRINT",EDGE,{"derivedFrom":sQuery(id+"F4.wireOp",EDGE,"E4.0.0.2")}),-1.0]])]});
            var Q141;
            Q141=makeQuery(id+"F4.imprint","IMPRINT",FACE,{"disambiguationData":[TD([[makeQuery(id+"F4.imprint","IMPRINT",EDGE,{"derivedFrom":sQuery(id+"F4.wireOp",EDGE,"E4.0.10.7")}),-1.0]])]});
            var Q142;
            Q142=makeQuery(id+"F4.imprint","IMPRINT",FACE,{"disambiguationData":[TD([[makeQuery(id+"F4.imprint","IMPRINT",EDGE,{"derivedFrom":sQuery(id+"F4.wireOp",EDGE,"E4.0.11.7")}),-1.0]])]});
            var Q143;
            Q143=makeQuery(id+"F4.imprint","IMPRINT",FACE,{"disambiguationData":[TD([[makeQuery(id+"F4.imprint","IMPRINT",EDGE,{"derivedFrom":sQuery(id+"F4.wireOp",EDGE,"E4.0.7.7")}),-1.0]])]});
            extrude(context, id + "F5", {"entities" : qUnion([Q0, Q1, Q2, Q3, Q4, Q5, Q6, Q7, Q8, Q9, Q10, Q11, Q12, Q13, Q14, Q15, Q16, Q17, Q18, Q19, Q20, Q21, Q22, Q23, Q24, Q25, Q26, Q27, Q28, Q29, Q30, Q31, Q32, Q33, Q34, Q35, Q36, Q37, Q38, Q39, Q40, Q41, Q42, Q43, Q44, Q45, Q46, Q47, Q48, Q49, Q50, Q51, Q52, Q53, Q54, Q55, Q56, Q57, Q58, Q59, Q60, Q61, Q62, Q63, Q64, Q65, Q66, Q67, Q68, Q69, Q70, Q71, Q72, Q73, Q74, Q75, Q76, Q77, Q78, Q79, Q80, Q81, Q82, Q83, Q84, Q85, Q86, Q87, Q88, Q89, Q90, Q91, Q92, Q93, Q94, Q95, Q96, Q97, Q98, Q99, Q100, Q101, Q102, Q103, Q104, Q105, Q106, Q107, Q108, Q109, Q110, Q111, Q112, Q113, Q114, Q115, Q116, Q117, Q118, Q119, Q120, Q121, Q122, Q123, Q124, Q125, Q126, Q127, Q128, Q129, Q130, Q131, Q132, Q133, Q134, Q135, Q136, Q137, Q138, Q139, Q140, Q141, Q142, Q143]), "operationType" : NewBodyOperationType.REMOVE, "endBound" : BoundingType.THROUGH_ALL, "oppositeDirection" : true, "depth" : 25 * mm});
        }
        {
            var Q0;
            Q0=makeQuery(id+"F1.opExtrude","CAP_FACE",FACE,{"disambiguationData":[OSD([sQuery(id+"F0.wireOp",EDGE,"E0.bottom"),sQuery(id+"F0.wireOp",EDGE,"E0.top"),sQuery(id+"F0.wireOp",EDGE,"E0.left"),sQuery(id+"F0.wireOp",EDGE,"E0.right")])],"isStart":false});
            var sketch = newSketch(context, id + "F6", { "sketchPlane" : qUnion([Q0])});
            skPoint(sketch, "E5", {"position": v(-201, 181) * mm});
            skPoint(sketch, "E6", {"position": v(-161, 181) * mm});
            skPoint(sketch, "E7", {"position": v(-161, 141) * mm});
            skPoint(sketch, "E8", {"position": v(-201, 141) * mm});
            skPoint(sketch, "E9", {"position": v(-39.5, 77) * mm});
            skPoint(sketch, "E10", {"position": v(-39.5, 62) * mm});
            skPoint(sketch, "E11", {"position": v(23.5, -4.5) * mm});
            skPoint(sketch, "E12", {"position": v(8.5, -4.5) * mm});
            skPoint(sketch, "E13", {"position": v(211, 66) * mm});
            skPoint(sketch, "E13.positionSnap0", {"position": v(201, 56) * mm});
            skPoint(sketch, "E14", {"position": v(199, 109) * mm});
            skSolve(sketch);
        }
        {
            var Q0;
            Q0=sQuery(id+"F6.wireOp",VERTEX,"E8");
            var Q1;
            Q1=sQuery(id+"F6.wireOp",VERTEX,"E7");
            var Q2;
            Q2=sQuery(id+"F6.wireOp",VERTEX,"E6");
            var Q3;
            Q3=sQuery(id+"F6.wireOp",VERTEX,"E5");
            var Q4;
            Q4=sQuery(id+"F6.wireOp",VERTEX,"E9");
            var Q5;
            Q5=sQuery(id+"F6.wireOp",VERTEX,"E10");
            var Q6;
            Q6=sQuery(id+"F6.wireOp",VERTEX,"E12");
            var Q7;
            Q7=sQuery(id+"F6.wireOp",VERTEX,"E11");
            var Q8;
            Q8=makeQuery(id+"F1.opExtrude","SWEPT_BODY",BODY,{"disambiguationData":[OSD([sQuery(id+"F0.wireOp",EDGE,"E0.bottom"),sQuery(id+"F0.wireOp",EDGE,"E0.top"),sQuery(id+"F0.wireOp",EDGE,"E0.left"),sQuery(id+"F0.wireOp",EDGE,"E0.right")])]});
            hole(context, id + "F7", {"style" : HoleStyle.SIMPLE, "endStyle" : HoleEndStyle.THROUGH, "standardTappedOrClearance" : lookupTablePath({ "standard" : "ISO", "size" : "5", "type" : "Drilled" }), "standardBlindInLast" : lookupTablePath({ "standard" : "ISO", "size" : "5", "type" : "Drilled" }), "holeDiameter" : 5 * mm, "tappedDepth" : 32 * mm, "tapClearance" : 3, "startFromSketch" : true, "locations" : qUnion([Q0, Q1, Q2, Q3, Q4, Q5, Q6, Q7]), "scope" : qUnion([Q8])});
        }
        {
            var Q0;
            Q0=sQuery(id+"F6.wireOp",VERTEX,"E14");
            var Q1;
            Q1=sQuery(id+"F6.wireOp",VERTEX,"E13");
            var Q2;
            Q2=makeQuery(id+"F1.opExtrude","SWEPT_BODY",BODY,{"disambiguationData":[OSD([sQuery(id+"F0.wireOp",EDGE,"E0.bottom"),sQuery(id+"F0.wireOp",EDGE,"E0.top"),sQuery(id+"F0.wireOp",EDGE,"E0.left"),sQuery(id+"F0.wireOp",EDGE,"E0.right")])]});
            hole(context, id + "F8", {"style" : HoleStyle.SIMPLE, "endStyle" : HoleEndStyle.BLIND, "standardTappedOrClearance" : lookupTablePath({ "standard" : "ISO", "size" : "4", "type" : "Drilled" }), "standardBlindInLast" : lookupTablePath({ "standard" : "ISO", "size" : "4", "type" : "Drilled" }), "holeDiameter" : 4 * mm, "holeDepth" : 34.4 * mm, "tappedDepth" : 32 * mm, "tapClearance" : 3, "startFromSketch" : true, "locations" : qUnion([Q0, Q1]), "scope" : qUnion([Q2])});
        }
    });
